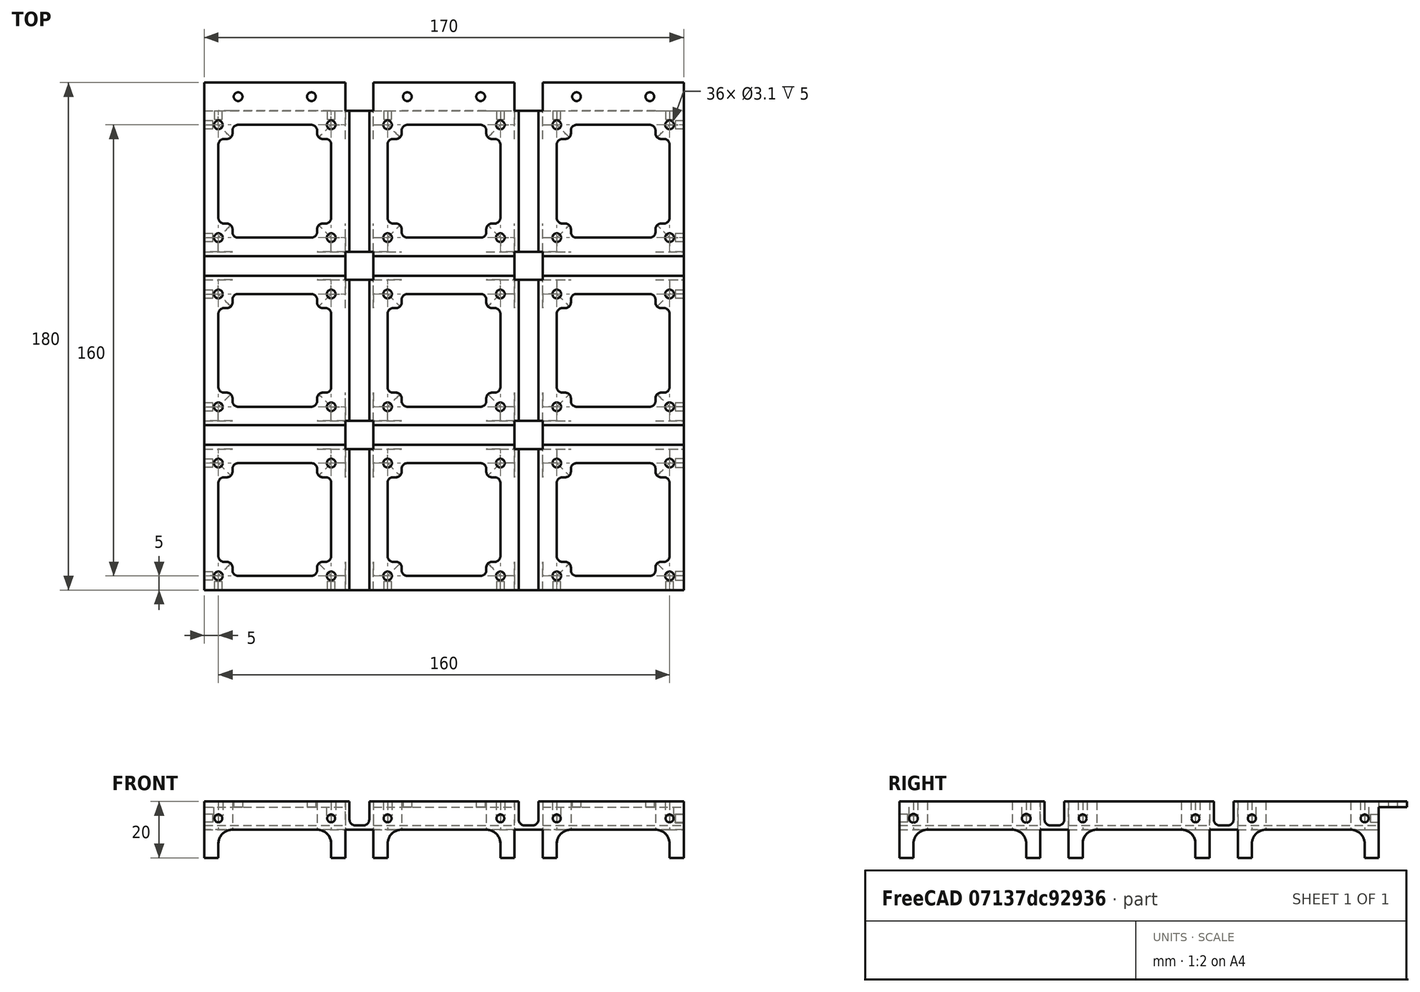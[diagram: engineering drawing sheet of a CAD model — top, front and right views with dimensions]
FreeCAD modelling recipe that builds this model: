
FCSTD DOCUMENT  (FreeCAD 0.20R29603 (Git))
Label: BackplaneLeft
License: All rights reserved
LicenseURL: http://en.wikipedia.org/wiki/All_rights_reserved
objects: Sketcher::SketchObject×59, PartDesign::Pocket×49, App::Link×13, PartDesign::Pad×10, PartDesign::Body×10, Part::Cylinder×2, Part::Cut×2, Part::Box×1, App::Part×1, Part::MultiFuse×1, Mesh::Feature×1
note: 193 computed .brp shape members not serialized (recipe doc carries the construction recipe); baked Part::Feature solids carry a one-line shape summary decoded from their .brp

FEATURE [Sketcher::SketchObject] Sketch
  FullyConstrained = true
  MapMode = 5
  Placement = pos=(0,0,0) rot=(0.57735,0.57735,0.57735;2.0944rad)
  Support = -> [YZ_Plane001]
  sketch-geometry (4):
    g0: LineSegment StartX=0 StartY=0 StartZ=0 EndX=10 EndY=0 EndZ=0
    g1: LineSegment StartX=10 StartY=0 StartZ=0 EndX=10 EndY=10 EndZ=0
    g2: LineSegment StartX=10 StartY=10 StartZ=0 EndX=0 EndY=10 EndZ=0
    g3: LineSegment StartX=0 StartY=10 StartZ=0 EndX=0 EndY=0 EndZ=0
  constraints (11):
    c: Coincident(g0,g1)
    c: Coincident(g1,g2)
    c: Coincident(g2,g3)
    c: Coincident(g3,g0)
    c: Horizontal(g0)
    c: Horizontal(g2)
    c: Vertical(g1)
    c: Vertical(g3)
    c: Coincident(g0,g-1)
    c: DistanceY(g3,g3) = 10
    c: DistanceX(g2,g2) = 10
FEATURE [PartDesign::Pad] Pad
  Direction = (1,-2e-16,3e-16)
  Length = 50
  Length2 = 10
  Placement = pos=(0,0,0) rot=(0.57735,0.57735,0.57735;2.0944rad)
  Profile = -> Sketch
  ReferenceAxis = -> Sketch [N_Axis]
  Type = 0
FEATURE [Sketcher::SketchObject] Sketch001
  ExternalGeometry = -> [Pad]
  FullyConstrained = true
  MapMode = 5
  Placement = pos=(0,0,0) rot=(0.57735,0.57735,-0.57735;4.18879rad)
  Support = -> [Pad]
  sketch-geometry (6):
    g0: LineSegment StartX=8.5 StartY=-10 StartZ=0 EndX=8.5 EndY=-3.5 EndZ=0
    g1: LineSegment StartX=6.5 StartY=-1.5 StartZ=0 EndX=3.5 EndY=-1.5 EndZ=0
    g2: LineSegment StartX=1.5 StartY=-3.5 StartZ=0 EndX=1.5 EndY=-10 EndZ=0
    g3: ArcOfCircle CenterX=6.5 CenterY=-3.5 CenterZ=0 NormalX=0 NormalY=0 NormalZ=1 AngleXU=0 Radius=2 StartAngle=1e-16 EndAngle=1.5708
    g4: ArcOfCircle CenterX=3.5 CenterY=-3.5 CenterZ=0 NormalX=0 NormalY=0 NormalZ=1 AngleXU=0 Radius=2 StartAngle=1.5708 EndAngle=3.14159
    g5: LineSegment StartX=1.5 StartY=-10 StartZ=0 EndX=8.5 EndY=-10 EndZ=0
  constraints (16):
    c: PointOnObject(g0,g-3)
    c: Vertical(g0)
    c: Horizontal(g1)
    c: PointOnObject(g2,g-3)
    c: Vertical(g2)
    c: Tangent(g0,g3) = -1.5708
    c: Tangent(g1,g3) = -1.5708
    c: Tangent(g1,g4) = -1.5708
    c: Tangent(g2,g4) = -1.5708
    c: Radius(g4) = 2
    c: Radius(g3) = 2
    c: Distance(g2,g-5) = 1.5
    c: Distance(g0,g-4) = 1.5
    c: Distance(g1,g-6) = 1.5
    c: Coincident(g5,g2)
    c: Coincident(g5,g0)
FEATURE [PartDesign::Pocket] Pocket
  BaseFeature = -> Pad
  Direction = (1,-4e-16,4e-16)
  Length = 5
  Length2 = 5
  Placement = pos=(0,0,0) rot=(0.57735,0.57735,0.57735;2.0944rad)
  Profile = -> Sketch001
  ReferenceAxis = -> Sketch001 [N_Axis]
  Type = 1
FEATURE [PartDesign::Body] Body  label="BackplaneChannel"
  Group = -> [Sketch,Pad,Sketch001,Pocket]
  Origin = -> Origin001
  Placement = pos=(0,50,10) rot=(0,0,1;0rad)
  Tip = -> Pocket
FEATURE [App::Link] Link008  label="BackplaneChannel001"
  LinkPlacement = pos=(60,50,10) rot=(0,0,1;0rad)
  LinkedObject = -> Body
  Placement = pos=(60,50,10) rot=(0,0,1;0rad)
FEATURE [App::Link] Link009  label="BackplaneChannel002"
  LinkPlacement = pos=(120,50,10) rot=(0,0,1;0rad)
  LinkedObject = -> Body
  Placement = pos=(120,50,10) rot=(0,0,1;0rad)
FEATURE [App::Link] Link010  label="BackplaneChannel003"
  LinkPlacement = pos=(0,110,10) rot=(0,0,1;0rad)
  LinkedObject = -> Body
  Placement = pos=(0,110,10) rot=(0,0,1;0rad)
FEATURE [App::Link] Link011  label="BackplaneChannel004"
  LinkPlacement = pos=(60,110,10) rot=(0,0,1;0rad)
  LinkedObject = -> Body
  Placement = pos=(60,110,10) rot=(0,0,1;0rad)
FEATURE [App::Link] Link012  label="BackplaneChannel005"
  LinkPlacement = pos=(120,110,10) rot=(0,0,1;0rad)
  LinkedObject = -> Body
  Placement = pos=(120,110,10) rot=(0,0,1;0rad)
FEATURE [App::Link] Link013  label="BackplaneChannel006"
  LinkPlacement = pos=(60,0,10) rot=(0,0,1;1.5708rad)
  LinkedObject = -> Body
  Placement = pos=(60,0,10) rot=(0,0,1;1.5708rad)
FEATURE [App::Link] Link014  label="BackplaneChannel007"
  LinkPlacement = pos=(120,0,10) rot=(0,0,1;1.5708rad)
  LinkedObject = -> Body
  Placement = pos=(120,0,10) rot=(0,0,1;1.5708rad)
FEATURE [App::Link] Link015  label="BackplaneChannel008"
  LinkPlacement = pos=(60,60,10) rot=(0,0,1;1.5708rad)
  LinkedObject = -> Body
  Placement = pos=(60,60,10) rot=(0,0,1;1.5708rad)
FEATURE [App::Link] Link016  label="BackplaneChannel009"
  LinkPlacement = pos=(60,120,10) rot=(0,0,1;1.5708rad)
  LinkedObject = -> Body
  Placement = pos=(60,120,10) rot=(0,0,1;1.5708rad)
FEATURE [App::Link] Link017  label="BackplaneChannel010"
  LinkPlacement = pos=(120,60,10) rot=(0,0,1;1.5708rad)
  LinkedObject = -> Body
  Placement = pos=(120,60,10) rot=(0,0,1;1.5708rad)
FEATURE [App::Link] Link018  label="BackplaneChannel011"
  LinkPlacement = pos=(120,120,10) rot=(0,0,1;1.5708rad)
  LinkedObject = -> Body
  Placement = pos=(120,120,10) rot=(0,0,1;1.5708rad)
FEATURE [Sketcher::SketchObject] Sketch002
  FullyConstrained = true
  MapMode = 5
  Support = -> [XY_Plane002]
  sketch-geometry (4):
    g0: LineSegment StartX=-25 StartY=25 StartZ=0 EndX=25 EndY=25 EndZ=0
    g1: LineSegment StartX=25 StartY=25 StartZ=0 EndX=25 EndY=-25 EndZ=0
    g2: LineSegment StartX=25 StartY=-25 StartZ=0 EndX=-25 EndY=-25 EndZ=0
    g3: LineSegment StartX=-25 StartY=-25 StartZ=0 EndX=-25 EndY=25 EndZ=0
  constraints (10):
    c: Coincident(g0,g1)
    c: Coincident(g1,g2)
    c: Coincident(g2,g3)
    c: Coincident(g3,g0)
    c: Horizontal(g0)
    c: Vertical(g3)
    c: Symmetric(g2,g1,g-2)
    c: Symmetric(g1,g0,g-1)
    c: DistanceY(g1,g1) = 50
    c: DistanceX(g2,g2) = 50
FEATURE [PartDesign::Pad] Pad001
  Direction = (0,0,1)
  Length = 20
  Length2 = 10
  Profile = -> Sketch002
  ReferenceAxis = -> Sketch002 [N_Axis]
  Type = 0
FEATURE [Sketcher::SketchObject] Sketch003
  ExternalGeometry = -> [Pad001]
  FullyConstrained = true
  MapMode = 5
  Placement = pos=(0,0,20) rot=(0,0,1;0rad)
  Support = -> [Pad001]
  sketch-geometry (36):
    g0: LineSegment StartX=-18 StartY=15 StartZ=0 EndX=-17 EndY=15 EndZ=0
    g1: LineSegment StartX=20 StartY=13 StartZ=0 EndX=20 EndY=-13 EndZ=0
    g2: LineSegment StartX=18 StartY=-15 StartZ=0 EndX=17 EndY=-15 EndZ=0
    g3: LineSegment StartX=-20 StartY=-13 StartZ=0 EndX=-20 EndY=13 EndZ=0
    g4: LineSegment StartX=-13 StartY=20 StartZ=0 EndX=13 EndY=20 EndZ=0
    g5: LineSegment StartX=15 StartY=18 StartZ=0 EndX=15 EndY=17 EndZ=0
    g6: LineSegment StartX=13 StartY=-20 StartZ=0 EndX=-13 EndY=-20 EndZ=0
    g7: LineSegment StartX=-15 StartY=-18 StartZ=0 EndX=-15 EndY=-17 EndZ=0
    g8: LineSegment StartX=17 StartY=15 StartZ=0 EndX=18 EndY=15 EndZ=0
    g9: LineSegment StartX=-15 StartY=17 StartZ=0 EndX=-15 EndY=18 EndZ=0
    g10: LineSegment StartX=-17 StartY=-15 StartZ=0 EndX=-18 EndY=-15 EndZ=0
    g11: LineSegment StartX=15 StartY=-17 StartZ=0 EndX=15 EndY=-18 EndZ=0
    g12: ArcOfCircle CenterX=-13 CenterY=-18 CenterZ=0 NormalX=0 NormalY=0 NormalZ=1 AngleXU=0 Radius=2 StartAngle=3.14159 EndAngle=4.71239
    g13: GeomPoint X=-15 Y=-20 Z=0
    g14: ArcOfCircle CenterX=13 CenterY=-18 CenterZ=0 NormalX=0 NormalY=0 NormalZ=1 AngleXU=0 Radius=2 StartAngle=4.71239 EndAngle=6.28319
    g15: GeomPoint X=15 Y=-20 Z=0
    g16: ArcOfCircle CenterX=17 CenterY=-17 CenterZ=0 NormalX=0 NormalY=0 NormalZ=1 AngleXU=0 Radius=2 StartAngle=1.5708 EndAngle=3.14159
    g17: GeomPoint X=15 Y=-15 Z=0
    g18: ArcOfCircle CenterX=18 CenterY=-13 CenterZ=0 NormalX=0 NormalY=0 NormalZ=1 AngleXU=0 Radius=2 StartAngle=4.71239 EndAngle=6.28319
    g19: GeomPoint X=20 Y=-15 Z=0
    g20: ArcOfCircle CenterX=18 CenterY=13 CenterZ=0 NormalX=0 NormalY=0 NormalZ=1 AngleXU=0 Radius=2 StartAngle=0 EndAngle=1.5708
    g21: GeomPoint X=20 Y=15 Z=0
    g22: ArcOfCircle CenterX=17 CenterY=17 CenterZ=0 NormalX=0 NormalY=0 NormalZ=1 AngleXU=0 Radius=2 StartAngle=3.14159 EndAngle=4.71239
    g23: GeomPoint X=15 Y=15 Z=0
    g24: ArcOfCircle CenterX=13 CenterY=18 CenterZ=0 NormalX=0 NormalY=0 NormalZ=1 AngleXU=0 Radius=2 StartAngle=4e-16 EndAngle=1.5708
    g25: GeomPoint X=15 Y=20 Z=0
    g26: ArcOfCircle CenterX=-13 CenterY=18 CenterZ=0 NormalX=0 NormalY=0 NormalZ=1 AngleXU=0 Radius=2 StartAngle=1.5708 EndAngle=3.14159
    g27: GeomPoint X=-15 Y=20 Z=0
    g28: ArcOfCircle CenterX=-17 CenterY=17 CenterZ=0 NormalX=0 NormalY=0 NormalZ=1 AngleXU=0 Radius=2 StartAngle=4.71239 EndAngle=6.28319
    g29: GeomPoint X=-15 Y=15 Z=0
    g30: ArcOfCircle CenterX=-18 CenterY=13 CenterZ=0 NormalX=0 NormalY=0 NormalZ=1 AngleXU=0 Radius=2 StartAngle=1.5708 EndAngle=3.14159
    g31: GeomPoint X=-20 Y=15 Z=0
    g32: ArcOfCircle CenterX=-18 CenterY=-13 CenterZ=0 NormalX=0 NormalY=0 NormalZ=1 AngleXU=0 Radius=2 StartAngle=3.14159 EndAngle=4.71239
    g33: GeomPoint X=-20 Y=-15 Z=0
    g34: ArcOfCircle CenterX=-17 CenterY=-17 CenterZ=0 NormalX=0 NormalY=0 NormalZ=1 AngleXU=0 Radius=2 StartAngle=0 EndAngle=1.5708
    g35: GeomPoint X=-15 Y=-15 Z=0
  constraints (80):
    c: Horizontal(g2)
    c: Vertical(g3)
    c: Symmetric(g21,g31,g-2)
    c: Symmetric(g21,g19,g-1)
    c: DistanceX(g31,g21) = 40
    c: DistanceY(g19,g21) = 30
    c: Horizontal(g4)
    c: Vertical(g7)
    c: Symmetric(g13,g15,g-2)
    c: Symmetric(g15,g25,g-1)
    c: DistanceY(g15,g25) = 40
    c: Vertical(g9)
    c: Vertical(g5)
    c: Vertical(g11)
    c: Horizontal(g10)
    c: Horizontal(g8)
    c: Horizontal(g0)
    c: DistanceX(g13,g15) = 30
    c: DistanceY(g33,g31) = 30
    c: DistanceX(g27,g25) = 30
    c: PointOnObject(g13,g7)
    c: PointOnObject(g13,g6)
    c: Tangent(g7,g12) = 1.5708
    c: Tangent(g6,g12) = 1.5708
    c: Radius(g12) = 2
    c: PointOnObject(g15,g11)
    c: PointOnObject(g15,g6)
    c: Tangent(g11,g14) = 1.5708
    c: Tangent(g6,g14) = 1.5708
    c: PointOnObject(g17,g11)
    c: PointOnObject(g17,g2)
    c: Tangent(g11,g16) = -1.5708
    c: Tangent(g2,g16) = -1.5708
    c: PointOnObject(g19,g2)
    c: PointOnObject(g19,g1)
    c: Tangent(g2,g18) = 1.5708
    c: Tangent(g1,g18) = 1.5708
    c: PointOnObject(g21,g1)
    c: PointOnObject(g21,g8)
    c: Tangent(g1,g20) = 1.5708
    c: Tangent(g8,g20) = 1.5708
    c: PointOnObject(g23,g8)
    c: PointOnObject(g23,g5)
    c: Tangent(g8,g22) = -1.5708
    c: Tangent(g5,g22) = -1.5708
    c: PointOnObject(g25,g5)
    c: PointOnObject(g25,g4)
    c: Tangent(g5,g24) = 1.5708
    c: Tangent(g4,g24) = 1.5708
    c: PointOnObject(g27,g9)
    c: PointOnObject(g27,g4)
    c: Tangent(g9,g26) = 1.5708
    c: Tangent(g4,g26) = 1.5708
    c: PointOnObject(g29,g9)
    c: PointOnObject(g29,g0)
    c: Tangent(g9,g28) = -1.5708
    c: Tangent(g0,g28) = -1.5708
    c: PointOnObject(g31,g0)
    c: PointOnObject(g31,g3)
    c: Tangent(g0,g30) = 1.5708
    c: Tangent(g3,g30) = 1.5708
    c: PointOnObject(g33,g3)
    c: PointOnObject(g33,g10)
    c: Tangent(g3,g32) = 1.5708
    c: Tangent(g10,g32) = 1.5708
    c: PointOnObject(g35,g10)
    c: PointOnObject(g35,g7)
    c: Tangent(g10,g34) = -1.5708
    c: Tangent(g7,g34) = -1.5708
    c: Radius(g34) = 2
    c: Radius(g32) = 2
    c: Radius(g30) = 2
    c: Radius(g28) = 2
    c: Radius(g26) = 2
    c: Radius(g24) = 2
    c: Radius(g22) = 2
    c: Radius(g20) = 2
    c: Radius(g18) = 2
    c: Radius(g16) = 2
    c: Radius(g14) = 2
FEATURE [PartDesign::Pocket] Pocket001
  BaseFeature = -> Pad001
  Direction = (0,0,-1)
  Length = 5
  Length2 = 5
  Profile = -> Sketch003
  ReferenceAxis = -> Sketch003 [N_Axis]
  Type = 1
FEATURE [Sketcher::SketchObject] Sketch004
  ExternalGeometry = -> [Pocket001]
  FullyConstrained = true
  MapMode = 5
  Placement = pos=(25,0,0) rot=(0.57735,0.57735,0.57735;2.0944rad)
  Support = -> [Pocket001]
  sketch-geometry (6):
    g0: LineSegment StartX=-15 StartY=10 StartZ=0 EndX=15 EndY=10 EndZ=0
    g1: LineSegment StartX=20 StartY=5 StartZ=0 EndX=20 EndY=0 EndZ=0
    g2: LineSegment StartX=20 StartY=0 StartZ=0 EndX=-20 EndY=0 EndZ=0
    g3: LineSegment StartX=-20 StartY=0 StartZ=0 EndX=-20 EndY=5 EndZ=0
    g4: ArcOfCircle CenterX=15 CenterY=5 CenterZ=0 NormalX=0 NormalY=0 NormalZ=1 AngleXU=0 Radius=5 StartAngle=1.11001e-11 EndAngle=1.5708
    g5: ArcOfCircle CenterX=-15 CenterY=5 CenterZ=0 NormalX=0 NormalY=0 NormalZ=1 AngleXU=0 Radius=5 StartAngle=1.5708 EndAngle=3.14159
  constraints (15):
    c: Coincident(g1,g2)
    c: Coincident(g2,g3)
    c: Vertical(g1)
    c: Vertical(g3)
    c: PointOnObject(g1,g-1)
    c: Tangent(g1,g4) = 1.5708
    c: Tangent(g0,g4) = 1.5708
    c: Tangent(g0,g5) = 1.5708
    c: Tangent(g3,g5) = 1.5708
    c: Horizontal(g0)
    c: DistanceX(g2,g2) = 40
    c: Symmetric(g2,g1,g-2)
    c: Distance(g-1,g0) = 10
    c: Radius(g5) = 5
    c: Radius(g4) = 5
FEATURE [PartDesign::Pocket] Pocket002
  BaseFeature = -> Pocket001
  Direction = (-1,0,0)
  Length = 5
  Length2 = 5
  Profile = -> Sketch004
  ReferenceAxis = -> Sketch004 [N_Axis]
  Type = 1
FEATURE [Sketcher::SketchObject] Sketch005
  FullyConstrained = true
  MapMode = 5
  Placement = pos=(0,-25,0) rot=(1,0,0;1.5708rad)
  Support = -> [Pocket001]
  sketch-geometry (6):
    g0: LineSegment StartX=-15 StartY=10 StartZ=0 EndX=15 EndY=10 EndZ=0
    g1: LineSegment StartX=20 StartY=5 StartZ=0 EndX=20 EndY=0 EndZ=0
    g2: LineSegment StartX=20 StartY=0 StartZ=0 EndX=-20 EndY=0 EndZ=0
    g3: LineSegment StartX=-20 StartY=0 StartZ=0 EndX=-20 EndY=5 EndZ=0
    g4: ArcOfCircle CenterX=15 CenterY=5 CenterZ=0 NormalX=0 NormalY=0 NormalZ=1 AngleXU=0 Radius=5 StartAngle=1.11e-11 EndAngle=1.5708
    g5: ArcOfCircle CenterX=-15 CenterY=5 CenterZ=0 NormalX=0 NormalY=0 NormalZ=1 AngleXU=0 Radius=5 StartAngle=1.5708 EndAngle=3.14159
  constraints (15):
    c: Coincident(g1,g2)
    c: Coincident(g2,g3)
    c: Horizontal(g0)
    c: Vertical(g1)
    c: Vertical(g3)
    c: Symmetric(g2,g1,g-2)
    c: PointOnObject(g1,g-1)
    c: Tangent(g0,g4) = 1.5708
    c: Tangent(g1,g4) = 1.5708
    c: Tangent(g0,g5) = 1.5708
    c: Tangent(g3,g5) = 1.5708
    c: DistanceX(g2,g2) = 40
    c: Distance(g-1,g0) = 10
    c: Radius(g5) = 5
    c: Radius(g4) = 5
FEATURE [PartDesign::Pocket] Pocket003
  BaseFeature = -> Pocket002
  Direction = (0,1,-2e-16)
  Length = 5
  Length2 = 5
  Profile = -> Sketch005
  ReferenceAxis = -> Sketch005 [N_Axis]
  Type = 1
FEATURE [Sketcher::SketchObject] Sketch009
  FullyConstrained = false
  MapMode = 5
  Placement = pos=(0,0,20) rot=(0,0,1;0rad)
  sketch-geometry (4):
    g0: Circle CenterX=-20 CenterY=20 CenterZ=0 NormalX=0 NormalY=0 NormalZ=1 AngleXU=0 Radius=1.55
    g1: Circle CenterX=20 CenterY=20 CenterZ=0 NormalX=0 NormalY=0 NormalZ=1 AngleXU=0 Radius=1.55
    g2: Circle CenterX=20 CenterY=-20 CenterZ=0 NormalX=0 NormalY=0 NormalZ=1 AngleXU=0 Radius=1.55
    g3: Circle CenterX=-20 CenterY=-20 CenterZ=0 NormalX=0 NormalY=0 NormalZ=1 AngleXU=0 Radius=1.55
  constraints (4):
    c: Diameter(g0) = 3.1
    c: Diameter(g1) = 3.1
    c: Diameter(g2) = 3.1
    c: Diameter(g3) = 3.1
FEATURE [PartDesign::Pocket] Pocket008
  BaseFeature = -> Pocket003
  Direction = (0,0,-1)
  Length = 5
  Length2 = 5
  Profile = -> Sketch009
  ReferenceAxis = -> Sketch009 [N_Axis]
  Type = 0
FEATURE [Sketcher::SketchObject] Sketch010
  FullyConstrained = true
  MapMode = 5
  Support = -> [XY_Plane003]
  sketch-geometry (4):
    g0: LineSegment StartX=-25 StartY=25 StartZ=0 EndX=25 EndY=25 EndZ=0
    g1: LineSegment StartX=25 StartY=25 StartZ=0 EndX=25 EndY=-25 EndZ=0
    g2: LineSegment StartX=25 StartY=-25 StartZ=0 EndX=-25 EndY=-25 EndZ=0
    g3: LineSegment StartX=-25 StartY=-25 StartZ=0 EndX=-25 EndY=25 EndZ=0
  constraints (10):
    c: Coincident(g0,g1)
    c: Coincident(g1,g2)
    c: Coincident(g2,g3)
    c: Coincident(g3,g0)
    c: Horizontal(g0)
    c: Vertical(g3)
    c: Symmetric(g2,g1,g-2)
    c: Symmetric(g1,g0,g-1)
    c: DistanceY(g1,g1) = 50
    c: DistanceX(g2,g2) = 50
FEATURE [PartDesign::Pad] Pad002
  Direction = (0,0,1)
  Length = 20
  Length2 = 10
  Profile = -> Sketch010
  ReferenceAxis = -> Sketch010 [N_Axis]
  Type = 0
FEATURE [Sketcher::SketchObject] Sketch011
  ExternalGeometry = -> [Pad002]
  FullyConstrained = true
  MapMode = 5
  Placement = pos=(0,0,20) rot=(0,0,1;0rad)
  Support = -> [Pad002]
  sketch-geometry (36):
    g0: LineSegment StartX=-18 StartY=15 StartZ=0 EndX=-17 EndY=15 EndZ=0
    g1: LineSegment StartX=20 StartY=13 StartZ=0 EndX=20 EndY=-13 EndZ=0
    g2: LineSegment StartX=18 StartY=-15 StartZ=0 EndX=17 EndY=-15 EndZ=0
    g3: LineSegment StartX=-20 StartY=-13 StartZ=0 EndX=-20 EndY=13 EndZ=0
    g4: LineSegment StartX=-13 StartY=20 StartZ=0 EndX=13 EndY=20 EndZ=0
    g5: LineSegment StartX=15 StartY=18 StartZ=0 EndX=15 EndY=17 EndZ=0
    g6: LineSegment StartX=13 StartY=-20 StartZ=0 EndX=-13 EndY=-20 EndZ=0
    g7: LineSegment StartX=-15 StartY=-18 StartZ=0 EndX=-15 EndY=-17 EndZ=0
    g8: LineSegment StartX=17 StartY=15 StartZ=0 EndX=18 EndY=15 EndZ=0
    g9: LineSegment StartX=-15 StartY=17 StartZ=0 EndX=-15 EndY=18 EndZ=0
    g10: LineSegment StartX=-17 StartY=-15 StartZ=0 EndX=-18 EndY=-15 EndZ=0
    g11: LineSegment StartX=15 StartY=-17 StartZ=0 EndX=15 EndY=-18 EndZ=0
    g12: ArcOfCircle CenterX=-13 CenterY=-18 CenterZ=0 NormalX=0 NormalY=0 NormalZ=1 AngleXU=0 Radius=2 StartAngle=3.14159 EndAngle=4.71239
    g13: GeomPoint X=-15 Y=-20 Z=0
    g14: ArcOfCircle CenterX=13 CenterY=-18 CenterZ=0 NormalX=0 NormalY=0 NormalZ=1 AngleXU=0 Radius=2 StartAngle=4.71239 EndAngle=6.28319
    g15: GeomPoint X=15 Y=-20 Z=0
    g16: ArcOfCircle CenterX=17 CenterY=-17 CenterZ=0 NormalX=0 NormalY=0 NormalZ=1 AngleXU=0 Radius=2 StartAngle=1.5708 EndAngle=3.14159
    g17: GeomPoint X=15 Y=-15 Z=0
    g18: ArcOfCircle CenterX=18 CenterY=-13 CenterZ=0 NormalX=0 NormalY=0 NormalZ=1 AngleXU=0 Radius=2 StartAngle=4.71239 EndAngle=6.28319
    g19: GeomPoint X=20 Y=-15 Z=0
    g20: ArcOfCircle CenterX=18 CenterY=13 CenterZ=0 NormalX=0 NormalY=0 NormalZ=1 AngleXU=0 Radius=2 StartAngle=0 EndAngle=1.5708
    g21: GeomPoint X=20 Y=15 Z=0
    g22: ArcOfCircle CenterX=17 CenterY=17 CenterZ=0 NormalX=0 NormalY=0 NormalZ=1 AngleXU=0 Radius=2 StartAngle=3.14159 EndAngle=4.71239
    g23: GeomPoint X=15 Y=15 Z=0
    g24: ArcOfCircle CenterX=13 CenterY=18 CenterZ=0 NormalX=0 NormalY=0 NormalZ=1 AngleXU=0 Radius=2 StartAngle=4e-16 EndAngle=1.5708
    g25: GeomPoint X=15 Y=20 Z=0
    g26: ArcOfCircle CenterX=-13 CenterY=18 CenterZ=0 NormalX=0 NormalY=0 NormalZ=1 AngleXU=0 Radius=2 StartAngle=1.5708 EndAngle=3.14159
    g27: GeomPoint X=-15 Y=20 Z=0
    g28: ArcOfCircle CenterX=-17 CenterY=17 CenterZ=0 NormalX=0 NormalY=0 NormalZ=1 AngleXU=0 Radius=2 StartAngle=4.71239 EndAngle=6.28319
    g29: GeomPoint X=-15 Y=15 Z=0
    g30: ArcOfCircle CenterX=-18 CenterY=13 CenterZ=0 NormalX=0 NormalY=0 NormalZ=1 AngleXU=0 Radius=2 StartAngle=1.5708 EndAngle=3.14159
    g31: GeomPoint X=-20 Y=15 Z=0
    g32: ArcOfCircle CenterX=-18 CenterY=-13 CenterZ=0 NormalX=0 NormalY=0 NormalZ=1 AngleXU=0 Radius=2 StartAngle=3.14159 EndAngle=4.71239
    g33: GeomPoint X=-20 Y=-15 Z=0
    g34: ArcOfCircle CenterX=-17 CenterY=-17 CenterZ=0 NormalX=0 NormalY=0 NormalZ=1 AngleXU=0 Radius=2 StartAngle=0 EndAngle=1.5708
    g35: GeomPoint X=-15 Y=-15 Z=0
  constraints (80):
    c: Horizontal(g2)
    c: Vertical(g3)
    c: Symmetric(g21,g31,g-2)
    c: Symmetric(g21,g19,g-1)
    c: DistanceX(g31,g21) = 40
    c: DistanceY(g19,g21) = 30
    c: Horizontal(g4)
    c: Vertical(g7)
    c: Symmetric(g13,g15,g-2)
    c: Symmetric(g15,g25,g-1)
    c: DistanceY(g15,g25) = 40
    c: Vertical(g9)
    c: Vertical(g5)
    c: Vertical(g11)
    c: Horizontal(g10)
    c: Horizontal(g8)
    c: Horizontal(g0)
    c: DistanceX(g13,g15) = 30
    c: DistanceY(g33,g31) = 30
    c: DistanceX(g27,g25) = 30
    c: PointOnObject(g13,g7)
    c: PointOnObject(g13,g6)
    c: Tangent(g7,g12) = 1.5708
    c: Tangent(g6,g12) = 1.5708
    c: Radius(g12) = 2
    c: PointOnObject(g15,g11)
    c: PointOnObject(g15,g6)
    c: Tangent(g11,g14) = 1.5708
    c: Tangent(g6,g14) = 1.5708
    c: PointOnObject(g17,g11)
    c: PointOnObject(g17,g2)
    c: Tangent(g11,g16) = -1.5708
    c: Tangent(g2,g16) = -1.5708
    c: PointOnObject(g19,g2)
    c: PointOnObject(g19,g1)
    c: Tangent(g2,g18) = 1.5708
    c: Tangent(g1,g18) = 1.5708
    c: PointOnObject(g21,g1)
    c: PointOnObject(g21,g8)
    c: Tangent(g1,g20) = 1.5708
    c: Tangent(g8,g20) = 1.5708
    c: PointOnObject(g23,g8)
    c: PointOnObject(g23,g5)
    c: Tangent(g8,g22) = -1.5708
    c: Tangent(g5,g22) = -1.5708
    c: PointOnObject(g25,g5)
    c: PointOnObject(g25,g4)
    c: Tangent(g5,g24) = 1.5708
    c: Tangent(g4,g24) = 1.5708
    c: PointOnObject(g27,g9)
    c: PointOnObject(g27,g4)
    c: Tangent(g9,g26) = 1.5708
    c: Tangent(g4,g26) = 1.5708
    c: PointOnObject(g29,g9)
    c: PointOnObject(g29,g0)
    c: Tangent(g9,g28) = -1.5708
    c: Tangent(g0,g28) = -1.5708
    c: PointOnObject(g31,g0)
    c: PointOnObject(g31,g3)
    c: Tangent(g0,g30) = 1.5708
    c: Tangent(g3,g30) = 1.5708
    c: PointOnObject(g33,g3)
    c: PointOnObject(g33,g10)
    c: Tangent(g3,g32) = 1.5708
    c: Tangent(g10,g32) = 1.5708
    c: PointOnObject(g35,g10)
    c: PointOnObject(g35,g7)
    c: Tangent(g10,g34) = -1.5708
    c: Tangent(g7,g34) = -1.5708
    c: Radius(g34) = 2
    c: Radius(g32) = 2
    c: Radius(g30) = 2
    c: Radius(g28) = 2
    c: Radius(g26) = 2
    c: Radius(g24) = 2
    c: Radius(g22) = 2
    c: Radius(g20) = 2
    c: Radius(g18) = 2
    c: Radius(g16) = 2
    c: Radius(g14) = 2
FEATURE [PartDesign::Pocket] Pocket009
  BaseFeature = -> Pad002
  Direction = (0,0,-1)
  Length = 5
  Length2 = 5
  Profile = -> Sketch011
  ReferenceAxis = -> Sketch011 [N_Axis]
  Type = 1
FEATURE [Sketcher::SketchObject] Sketch012
  ExternalGeometry = -> [Pocket009]
  FullyConstrained = true
  MapMode = 5
  Placement = pos=(25,0,0) rot=(0.57735,0.57735,0.57735;2.0944rad)
  Support = -> [Pocket009]
  sketch-geometry (6):
    g0: LineSegment StartX=-15 StartY=10 StartZ=0 EndX=15 EndY=10 EndZ=0
    g1: LineSegment StartX=20 StartY=5 StartZ=0 EndX=20 EndY=0 EndZ=0
    g2: LineSegment StartX=20 StartY=0 StartZ=0 EndX=-20 EndY=0 EndZ=0
    g3: LineSegment StartX=-20 StartY=0 StartZ=0 EndX=-20 EndY=5 EndZ=0
    g4: ArcOfCircle CenterX=15 CenterY=5 CenterZ=0 NormalX=0 NormalY=0 NormalZ=1 AngleXU=0 Radius=5 StartAngle=1.11001e-11 EndAngle=1.5708
    g5: ArcOfCircle CenterX=-15 CenterY=5 CenterZ=0 NormalX=0 NormalY=0 NormalZ=1 AngleXU=0 Radius=5 StartAngle=1.5708 EndAngle=3.14159
  constraints (15):
    c: Coincident(g1,g2)
    c: Coincident(g2,g3)
    c: Vertical(g1)
    c: Vertical(g3)
    c: PointOnObject(g1,g-1)
    c: Tangent(g1,g4) = 1.5708
    c: Tangent(g0,g4) = 1.5708
    c: Tangent(g0,g5) = 1.5708
    c: Tangent(g3,g5) = 1.5708
    c: Horizontal(g0)
    c: DistanceX(g2,g2) = 40
    c: Symmetric(g2,g1,g-2)
    c: Distance(g-1,g0) = 10
    c: Radius(g5) = 5
    c: Radius(g4) = 5
FEATURE [PartDesign::Pocket] Pocket010
  BaseFeature = -> Pocket009
  Direction = (-1,0,0)
  Length = 5
  Length2 = 5
  Profile = -> Sketch012
  ReferenceAxis = -> Sketch012 [N_Axis]
  Type = 1
FEATURE [Sketcher::SketchObject] Sketch013
  FullyConstrained = true
  MapMode = 5
  Placement = pos=(0,-25,0) rot=(1,0,0;1.5708rad)
  Support = -> [Pocket009]
  sketch-geometry (6):
    g0: LineSegment StartX=-15 StartY=10 StartZ=0 EndX=15 EndY=10 EndZ=0
    g1: LineSegment StartX=20 StartY=5 StartZ=0 EndX=20 EndY=0 EndZ=0
    g2: LineSegment StartX=20 StartY=0 StartZ=0 EndX=-20 EndY=0 EndZ=0
    g3: LineSegment StartX=-20 StartY=0 StartZ=0 EndX=-20 EndY=5 EndZ=0
    g4: ArcOfCircle CenterX=15 CenterY=5 CenterZ=0 NormalX=0 NormalY=0 NormalZ=1 AngleXU=0 Radius=5 StartAngle=1.11e-11 EndAngle=1.5708
    g5: ArcOfCircle CenterX=-15 CenterY=5 CenterZ=0 NormalX=0 NormalY=0 NormalZ=1 AngleXU=0 Radius=5 StartAngle=1.5708 EndAngle=3.14159
  constraints (15):
    c: Coincident(g1,g2)
    c: Coincident(g2,g3)
    c: Horizontal(g0)
    c: Vertical(g1)
    c: Vertical(g3)
    c: Symmetric(g2,g1,g-2)
    c: PointOnObject(g1,g-1)
    c: Tangent(g0,g4) = 1.5708
    c: Tangent(g1,g4) = 1.5708
    c: Tangent(g0,g5) = 1.5708
    c: Tangent(g3,g5) = 1.5708
    c: DistanceX(g2,g2) = 40
    c: Distance(g-1,g0) = 10
    c: Radius(g5) = 5
    c: Radius(g4) = 5
FEATURE [PartDesign::Pocket] Pocket011
  BaseFeature = -> Pocket010
  Direction = (0,1,-2e-16)
  Length = 5
  Length2 = 5
  Profile = -> Sketch013
  ReferenceAxis = -> Sketch013 [N_Axis]
  Type = 1
FEATURE [Sketcher::SketchObject] Sketch014
  FullyConstrained = false
  MapMode = 5
  Placement = pos=(0,0,20) rot=(0,0,1;0rad)
  sketch-geometry (4):
    g0: Circle CenterX=-20 CenterY=20 CenterZ=0 NormalX=0 NormalY=0 NormalZ=1 AngleXU=0 Radius=1.55
    g1: Circle CenterX=20 CenterY=20 CenterZ=0 NormalX=0 NormalY=0 NormalZ=1 AngleXU=0 Radius=1.55
    g2: Circle CenterX=20 CenterY=-20 CenterZ=0 NormalX=0 NormalY=0 NormalZ=1 AngleXU=0 Radius=1.55
    g3: Circle CenterX=-20 CenterY=-20 CenterZ=0 NormalX=0 NormalY=0 NormalZ=1 AngleXU=0 Radius=1.55
  constraints (4):
    c: Diameter(g0) = 3.1
    c: Diameter(g1) = 3.1
    c: Diameter(g2) = 3.1
    c: Diameter(g3) = 3.1
FEATURE [PartDesign::Pocket] Pocket012
  BaseFeature = -> Pocket011
  Direction = (0,0,-1)
  Length = 5
  Length2 = 5
  Profile = -> Sketch014
  ReferenceAxis = -> Sketch014 [N_Axis]
  Type = 0
FEATURE [PartDesign::Body] Body003  label="BackplaneBlock001"
  Group = -> [Sketch010,Pad002,Sketch011,Pocket009,Sketch012,Sketch013,Pocket010,Pocket011,Sketch014,Pocket012]
  Origin = -> Origin003
  Placement = pos=(85,85,0) rot=(0,0,1;0rad)
  Tip = -> Pocket012
FEATURE [Sketcher::SketchObject] Sketch015
  ExternalGeometry = -> [Pocket008]
  FullyConstrained = true
  MapMode = 5
  Placement = pos=(0,-25,0) rot=(1,0,0;1.5708rad)
  Support = -> [Pocket008]
  sketch-geometry (2):
    g0: Circle CenterX=-20 CenterY=14 CenterZ=0 NormalX=0 NormalY=0 NormalZ=1 AngleXU=0 Radius=1.4
    g1: Circle CenterX=20 CenterY=14 CenterZ=0 NormalX=0 NormalY=0 NormalZ=1 AngleXU=0 Radius=1.4
  constraints (6):
    c: Diameter(g0) = 2.8
    c: Diameter(g1) = 2.8
    c: Distance(g0,g-5) = 5
    c: Distance(g0,g-3) = 6
    c: Distance(g1,g-3) = 6
    c: Distance(g1,g-4) = 5
FEATURE [PartDesign::Pocket] Pocket013
  BaseFeature = -> Pocket008
  Direction = (0,1,-2e-16)
  Length = 3
  Length2 = 5
  Profile = -> Sketch015
  ReferenceAxis = -> Sketch015 [N_Axis]
  Type = 0
FEATURE [Sketcher::SketchObject] Sketch016
  FullyConstrained = true
  MapMode = 5
  Support = -> [XY_Plane004]
  sketch-geometry (4):
    g0: LineSegment StartX=-25 StartY=25 StartZ=0 EndX=25 EndY=25 EndZ=0
    g1: LineSegment StartX=25 StartY=25 StartZ=0 EndX=25 EndY=-25 EndZ=0
    g2: LineSegment StartX=25 StartY=-25 StartZ=0 EndX=-25 EndY=-25 EndZ=0
    g3: LineSegment StartX=-25 StartY=-25 StartZ=0 EndX=-25 EndY=25 EndZ=0
  constraints (10):
    c: Coincident(g0,g1)
    c: Coincident(g1,g2)
    c: Coincident(g2,g3)
    c: Coincident(g3,g0)
    c: Horizontal(g0)
    c: Vertical(g3)
    c: Symmetric(g2,g1,g-2)
    c: Symmetric(g1,g0,g-1)
    c: DistanceY(g1,g1) = 50
    c: DistanceX(g2,g2) = 50
FEATURE [PartDesign::Pad] Pad003
  Direction = (0,0,1)
  Length = 20
  Length2 = 10
  Profile = -> Sketch016
  ReferenceAxis = -> Sketch016 [N_Axis]
  Type = 0
FEATURE [Sketcher::SketchObject] Sketch017
  ExternalGeometry = -> [Pad003]
  FullyConstrained = true
  MapMode = 5
  Placement = pos=(0,0,20) rot=(0,0,1;0rad)
  Support = -> [Pad003]
  sketch-geometry (36):
    g0: LineSegment StartX=-18 StartY=15 StartZ=0 EndX=-17 EndY=15 EndZ=0
    g1: LineSegment StartX=20 StartY=13 StartZ=0 EndX=20 EndY=-13 EndZ=0
    g2: LineSegment StartX=18 StartY=-15 StartZ=0 EndX=17 EndY=-15 EndZ=0
    g3: LineSegment StartX=-20 StartY=-13 StartZ=0 EndX=-20 EndY=13 EndZ=0
    g4: LineSegment StartX=-13 StartY=20 StartZ=0 EndX=13 EndY=20 EndZ=0
    g5: LineSegment StartX=15 StartY=18 StartZ=0 EndX=15 EndY=17 EndZ=0
    g6: LineSegment StartX=13 StartY=-20 StartZ=0 EndX=-13 EndY=-20 EndZ=0
    g7: LineSegment StartX=-15 StartY=-18 StartZ=0 EndX=-15 EndY=-17 EndZ=0
    g8: LineSegment StartX=17 StartY=15 StartZ=0 EndX=18 EndY=15 EndZ=0
    g9: LineSegment StartX=-15 StartY=17 StartZ=0 EndX=-15 EndY=18 EndZ=0
    g10: LineSegment StartX=-17 StartY=-15 StartZ=0 EndX=-18 EndY=-15 EndZ=0
    g11: LineSegment StartX=15 StartY=-17 StartZ=0 EndX=15 EndY=-18 EndZ=0
    g12: ArcOfCircle CenterX=-13 CenterY=-18 CenterZ=0 NormalX=0 NormalY=0 NormalZ=1 AngleXU=0 Radius=2 StartAngle=3.14159 EndAngle=4.71239
    g13: GeomPoint X=-15 Y=-20 Z=0
    g14: ArcOfCircle CenterX=13 CenterY=-18 CenterZ=0 NormalX=0 NormalY=0 NormalZ=1 AngleXU=0 Radius=2 StartAngle=4.71239 EndAngle=6.28319
    g15: GeomPoint X=15 Y=-20 Z=0
    g16: ArcOfCircle CenterX=17 CenterY=-17 CenterZ=0 NormalX=0 NormalY=0 NormalZ=1 AngleXU=0 Radius=2 StartAngle=1.5708 EndAngle=3.14159
    g17: GeomPoint X=15 Y=-15 Z=0
    g18: ArcOfCircle CenterX=18 CenterY=-13 CenterZ=0 NormalX=0 NormalY=0 NormalZ=1 AngleXU=0 Radius=2 StartAngle=4.71239 EndAngle=6.28319
    g19: GeomPoint X=20 Y=-15 Z=0
    g20: ArcOfCircle CenterX=18 CenterY=13 CenterZ=0 NormalX=0 NormalY=0 NormalZ=1 AngleXU=0 Radius=2 StartAngle=0 EndAngle=1.5708
    g21: GeomPoint X=20 Y=15 Z=0
    g22: ArcOfCircle CenterX=17 CenterY=17 CenterZ=0 NormalX=0 NormalY=0 NormalZ=1 AngleXU=0 Radius=2 StartAngle=3.14159 EndAngle=4.71239
    g23: GeomPoint X=15 Y=15 Z=0
    g24: ArcOfCircle CenterX=13 CenterY=18 CenterZ=0 NormalX=0 NormalY=0 NormalZ=1 AngleXU=0 Radius=2 StartAngle=4e-16 EndAngle=1.5708
    g25: GeomPoint X=15 Y=20 Z=0
    g26: ArcOfCircle CenterX=-13 CenterY=18 CenterZ=0 NormalX=0 NormalY=0 NormalZ=1 AngleXU=0 Radius=2 StartAngle=1.5708 EndAngle=3.14159
    g27: GeomPoint X=-15 Y=20 Z=0
    g28: ArcOfCircle CenterX=-17 CenterY=17 CenterZ=0 NormalX=0 NormalY=0 NormalZ=1 AngleXU=0 Radius=2 StartAngle=4.71239 EndAngle=6.28319
    g29: GeomPoint X=-15 Y=15 Z=0
    g30: ArcOfCircle CenterX=-18 CenterY=13 CenterZ=0 NormalX=0 NormalY=0 NormalZ=1 AngleXU=0 Radius=2 StartAngle=1.5708 EndAngle=3.14159
    g31: GeomPoint X=-20 Y=15 Z=0
    g32: ArcOfCircle CenterX=-18 CenterY=-13 CenterZ=0 NormalX=0 NormalY=0 NormalZ=1 AngleXU=0 Radius=2 StartAngle=3.14159 EndAngle=4.71239
    g33: GeomPoint X=-20 Y=-15 Z=0
    g34: ArcOfCircle CenterX=-17 CenterY=-17 CenterZ=0 NormalX=0 NormalY=0 NormalZ=1 AngleXU=0 Radius=2 StartAngle=0 EndAngle=1.5708
    g35: GeomPoint X=-15 Y=-15 Z=0
  constraints (80):
    c: Horizontal(g2)
    c: Vertical(g3)
    c: Symmetric(g21,g31,g-2)
    c: Symmetric(g21,g19,g-1)
    c: DistanceX(g31,g21) = 40
    c: DistanceY(g19,g21) = 30
    c: Horizontal(g4)
    c: Vertical(g7)
    c: Symmetric(g13,g15,g-2)
    c: Symmetric(g15,g25,g-1)
    c: DistanceY(g15,g25) = 40
    c: Vertical(g9)
    c: Vertical(g5)
    c: Vertical(g11)
    c: Horizontal(g10)
    c: Horizontal(g8)
    c: Horizontal(g0)
    c: DistanceX(g13,g15) = 30
    c: DistanceY(g33,g31) = 30
    c: DistanceX(g27,g25) = 30
    c: PointOnObject(g13,g7)
    c: PointOnObject(g13,g6)
    c: Tangent(g7,g12) = 1.5708
    c: Tangent(g6,g12) = 1.5708
    c: Radius(g12) = 2
    c: PointOnObject(g15,g11)
    c: PointOnObject(g15,g6)
    c: Tangent(g11,g14) = 1.5708
    c: Tangent(g6,g14) = 1.5708
    c: PointOnObject(g17,g11)
    c: PointOnObject(g17,g2)
    c: Tangent(g11,g16) = -1.5708
    c: Tangent(g2,g16) = -1.5708
    c: PointOnObject(g19,g2)
    c: PointOnObject(g19,g1)
    c: Tangent(g2,g18) = 1.5708
    c: Tangent(g1,g18) = 1.5708
    c: PointOnObject(g21,g1)
    c: PointOnObject(g21,g8)
    c: Tangent(g1,g20) = 1.5708
    c: Tangent(g8,g20) = 1.5708
    c: PointOnObject(g23,g8)
    c: PointOnObject(g23,g5)
    c: Tangent(g8,g22) = -1.5708
    c: Tangent(g5,g22) = -1.5708
    c: PointOnObject(g25,g5)
    c: PointOnObject(g25,g4)
    c: Tangent(g5,g24) = 1.5708
    c: Tangent(g4,g24) = 1.5708
    c: PointOnObject(g27,g9)
    c: PointOnObject(g27,g4)
    c: Tangent(g9,g26) = 1.5708
    c: Tangent(g4,g26) = 1.5708
    c: PointOnObject(g29,g9)
    c: PointOnObject(g29,g0)
    c: Tangent(g9,g28) = -1.5708
    c: Tangent(g0,g28) = -1.5708
    c: PointOnObject(g31,g0)
    c: PointOnObject(g31,g3)
    c: Tangent(g0,g30) = 1.5708
    c: Tangent(g3,g30) = 1.5708
    c: PointOnObject(g33,g3)
    c: PointOnObject(g33,g10)
    c: Tangent(g3,g32) = 1.5708
    c: Tangent(g10,g32) = 1.5708
    c: PointOnObject(g35,g10)
    c: PointOnObject(g35,g7)
    c: Tangent(g10,g34) = -1.5708
    c: Tangent(g7,g34) = -1.5708
    c: Radius(g34) = 2
    c: Radius(g32) = 2
    c: Radius(g30) = 2
    c: Radius(g28) = 2
    c: Radius(g26) = 2
    c: Radius(g24) = 2
    c: Radius(g22) = 2
    c: Radius(g20) = 2
    c: Radius(g18) = 2
    c: Radius(g16) = 2
    c: Radius(g14) = 2
FEATURE [PartDesign::Pocket] Pocket014
  BaseFeature = -> Pad003
  Direction = (0,0,-1)
  Length = 5
  Length2 = 5
  Profile = -> Sketch017
  ReferenceAxis = -> Sketch017 [N_Axis]
  Type = 1
FEATURE [Sketcher::SketchObject] Sketch018
  ExternalGeometry = -> [Pocket014]
  FullyConstrained = true
  MapMode = 5
  Placement = pos=(25,0,0) rot=(0.57735,0.57735,0.57735;2.0944rad)
  Support = -> [Pocket014]
  sketch-geometry (6):
    g0: LineSegment StartX=-15 StartY=10 StartZ=0 EndX=15 EndY=10 EndZ=0
    g1: LineSegment StartX=20 StartY=5 StartZ=0 EndX=20 EndY=0 EndZ=0
    g2: LineSegment StartX=20 StartY=0 StartZ=0 EndX=-20 EndY=0 EndZ=0
    g3: LineSegment StartX=-20 StartY=0 StartZ=0 EndX=-20 EndY=5 EndZ=0
    g4: ArcOfCircle CenterX=15 CenterY=5 CenterZ=0 NormalX=0 NormalY=0 NormalZ=1 AngleXU=0 Radius=5 StartAngle=1.11001e-11 EndAngle=1.5708
    g5: ArcOfCircle CenterX=-15 CenterY=5 CenterZ=0 NormalX=0 NormalY=0 NormalZ=1 AngleXU=0 Radius=5 StartAngle=1.5708 EndAngle=3.14159
  constraints (15):
    c: Coincident(g1,g2)
    c: Coincident(g2,g3)
    c: Vertical(g1)
    c: Vertical(g3)
    c: PointOnObject(g1,g-1)
    c: Tangent(g1,g4) = 1.5708
    c: Tangent(g0,g4) = 1.5708
    c: Tangent(g0,g5) = 1.5708
    c: Tangent(g3,g5) = 1.5708
    c: Horizontal(g0)
    c: DistanceX(g2,g2) = 40
    c: Symmetric(g2,g1,g-2)
    c: Distance(g-1,g0) = 10
    c: Radius(g5) = 5
    c: Radius(g4) = 5
FEATURE [PartDesign::Pocket] Pocket015
  BaseFeature = -> Pocket014
  Direction = (-1,0,0)
  Length = 5
  Length2 = 5
  Profile = -> Sketch018
  ReferenceAxis = -> Sketch018 [N_Axis]
  Type = 1
FEATURE [Sketcher::SketchObject] Sketch019
  FullyConstrained = true
  MapMode = 5
  Placement = pos=(0,-25,0) rot=(1,0,0;1.5708rad)
  Support = -> [Pocket014]
  sketch-geometry (6):
    g0: LineSegment StartX=-15 StartY=10 StartZ=0 EndX=15 EndY=10 EndZ=0
    g1: LineSegment StartX=20 StartY=5 StartZ=0 EndX=20 EndY=0 EndZ=0
    g2: LineSegment StartX=20 StartY=0 StartZ=0 EndX=-20 EndY=0 EndZ=0
    g3: LineSegment StartX=-20 StartY=0 StartZ=0 EndX=-20 EndY=5 EndZ=0
    g4: ArcOfCircle CenterX=15 CenterY=5 CenterZ=0 NormalX=0 NormalY=0 NormalZ=1 AngleXU=0 Radius=5 StartAngle=1.11e-11 EndAngle=1.5708
    g5: ArcOfCircle CenterX=-15 CenterY=5 CenterZ=0 NormalX=0 NormalY=0 NormalZ=1 AngleXU=0 Radius=5 StartAngle=1.5708 EndAngle=3.14159
  constraints (15):
    c: Coincident(g1,g2)
    c: Coincident(g2,g3)
    c: Horizontal(g0)
    c: Vertical(g1)
    c: Vertical(g3)
    c: Symmetric(g2,g1,g-2)
    c: PointOnObject(g1,g-1)
    c: Tangent(g0,g4) = 1.5708
    c: Tangent(g1,g4) = 1.5708
    c: Tangent(g0,g5) = 1.5708
    c: Tangent(g3,g5) = 1.5708
    c: DistanceX(g2,g2) = 40
    c: Distance(g-1,g0) = 10
    c: Radius(g5) = 5
    c: Radius(g4) = 5
FEATURE [PartDesign::Pocket] Pocket016
  BaseFeature = -> Pocket015
  Direction = (0,1,-2e-16)
  Length = 5
  Length2 = 5
  Profile = -> Sketch019
  ReferenceAxis = -> Sketch019 [N_Axis]
  Type = 1
FEATURE [Sketcher::SketchObject] Sketch020
  FullyConstrained = false
  MapMode = 5
  Placement = pos=(0,0,20) rot=(0,0,1;0rad)
  sketch-geometry (4):
    g0: Circle CenterX=-20 CenterY=20 CenterZ=0 NormalX=0 NormalY=0 NormalZ=1 AngleXU=0 Radius=1.55
    g1: Circle CenterX=20 CenterY=20 CenterZ=0 NormalX=0 NormalY=0 NormalZ=1 AngleXU=0 Radius=1.55
    g2: Circle CenterX=20 CenterY=-20 CenterZ=0 NormalX=0 NormalY=0 NormalZ=1 AngleXU=0 Radius=1.55
    g3: Circle CenterX=-20 CenterY=-20 CenterZ=0 NormalX=0 NormalY=0 NormalZ=1 AngleXU=0 Radius=1.55
  constraints (4):
    c: Diameter(g0) = 3.1
    c: Diameter(g1) = 3.1
    c: Diameter(g2) = 3.1
    c: Diameter(g3) = 3.1
FEATURE [PartDesign::Pocket] Pocket017
  BaseFeature = -> Pocket016
  Direction = (0,0,-1)
  Length = 5
  Length2 = 5
  Profile = -> Sketch020
  ReferenceAxis = -> Sketch020 [N_Axis]
  Type = 0
FEATURE [Sketcher::SketchObject] Sketch021
  ExternalGeometry = -> [Pocket017]
  FullyConstrained = true
  MapMode = 5
  Placement = pos=(0,-25,0) rot=(1,0,0;1.5708rad)
  Support = -> [Pocket017]
  sketch-geometry (2):
    g0: Circle CenterX=-20 CenterY=14 CenterZ=0 NormalX=0 NormalY=0 NormalZ=1 AngleXU=0 Radius=1.4
    g1: Circle CenterX=20 CenterY=14 CenterZ=0 NormalX=0 NormalY=0 NormalZ=1 AngleXU=0 Radius=1.4
  constraints (6):
    c: Diameter(g0) = 2.8
    c: Diameter(g1) = 2.8
    c: Distance(g0,g-5) = 5
    c: Distance(g0,g-3) = 6
    c: Distance(g1,g-3) = 6
    c: Distance(g1,g-4) = 5
FEATURE [PartDesign::Pocket] Pocket018
  BaseFeature = -> Pocket017
  Direction = (0,1,-2e-16)
  Length = 3
  Length2 = 5
  Profile = -> Sketch021
  ReferenceAxis = -> Sketch021 [N_Axis]
  Type = 0
FEATURE [PartDesign::Body] Body004  label="BackplaneBlock002"
  Group = -> [Sketch016,Pad003,Sketch017,Pocket014,Sketch018,Sketch019,Pocket015,Pocket016,Sketch020,Pocket017,Sketch021,Pocket018]
  Origin = -> Origin004
  Placement = pos=(85,145,0) rot=(0,0,1;3.14159rad)
  Tip = -> Pocket018
FEATURE [Sketcher::SketchObject] Sketch022
  FullyConstrained = true
  MapMode = 5
  Support = -> [XY_Plane005]
  sketch-geometry (4):
    g0: LineSegment StartX=-25 StartY=25 StartZ=0 EndX=25 EndY=25 EndZ=0
    g1: LineSegment StartX=25 StartY=25 StartZ=0 EndX=25 EndY=-25 EndZ=0
    g2: LineSegment StartX=25 StartY=-25 StartZ=0 EndX=-25 EndY=-25 EndZ=0
    g3: LineSegment StartX=-25 StartY=-25 StartZ=0 EndX=-25 EndY=25 EndZ=0
  constraints (10):
    c: Coincident(g0,g1)
    c: Coincident(g1,g2)
    c: Coincident(g2,g3)
    c: Coincident(g3,g0)
    c: Horizontal(g0)
    c: Vertical(g3)
    c: Symmetric(g2,g1,g-2)
    c: Symmetric(g1,g0,g-1)
    c: DistanceY(g1,g1) = 50
    c: DistanceX(g2,g2) = 50
FEATURE [PartDesign::Pad] Pad004
  Direction = (0,0,1)
  Length = 20
  Length2 = 10
  Profile = -> Sketch022
  ReferenceAxis = -> Sketch022 [N_Axis]
  Type = 0
FEATURE [Sketcher::SketchObject] Sketch023
  ExternalGeometry = -> [Pad004]
  FullyConstrained = true
  MapMode = 5
  Placement = pos=(0,0,20) rot=(0,0,1;0rad)
  Support = -> [Pad004]
  sketch-geometry (36):
    g0: LineSegment StartX=-18 StartY=15 StartZ=0 EndX=-17 EndY=15 EndZ=0
    g1: LineSegment StartX=20 StartY=13 StartZ=0 EndX=20 EndY=-13 EndZ=0
    g2: LineSegment StartX=18 StartY=-15 StartZ=0 EndX=17 EndY=-15 EndZ=0
    g3: LineSegment StartX=-20 StartY=-13 StartZ=0 EndX=-20 EndY=13 EndZ=0
    g4: LineSegment StartX=-13 StartY=20 StartZ=0 EndX=13 EndY=20 EndZ=0
    g5: LineSegment StartX=15 StartY=18 StartZ=0 EndX=15 EndY=17 EndZ=0
    g6: LineSegment StartX=13 StartY=-20 StartZ=0 EndX=-13 EndY=-20 EndZ=0
    g7: LineSegment StartX=-15 StartY=-18 StartZ=0 EndX=-15 EndY=-17 EndZ=0
    g8: LineSegment StartX=17 StartY=15 StartZ=0 EndX=18 EndY=15 EndZ=0
    g9: LineSegment StartX=-15 StartY=17 StartZ=0 EndX=-15 EndY=18 EndZ=0
    g10: LineSegment StartX=-17 StartY=-15 StartZ=0 EndX=-18 EndY=-15 EndZ=0
    g11: LineSegment StartX=15 StartY=-17 StartZ=0 EndX=15 EndY=-18 EndZ=0
    g12: ArcOfCircle CenterX=-13 CenterY=-18 CenterZ=0 NormalX=0 NormalY=0 NormalZ=1 AngleXU=0 Radius=2 StartAngle=3.14159 EndAngle=4.71239
    g13: GeomPoint X=-15 Y=-20 Z=0
    g14: ArcOfCircle CenterX=13 CenterY=-18 CenterZ=0 NormalX=0 NormalY=0 NormalZ=1 AngleXU=0 Radius=2 StartAngle=4.71239 EndAngle=6.28319
    g15: GeomPoint X=15 Y=-20 Z=0
    g16: ArcOfCircle CenterX=17 CenterY=-17 CenterZ=0 NormalX=0 NormalY=0 NormalZ=1 AngleXU=0 Radius=2 StartAngle=1.5708 EndAngle=3.14159
    g17: GeomPoint X=15 Y=-15 Z=0
    g18: ArcOfCircle CenterX=18 CenterY=-13 CenterZ=0 NormalX=0 NormalY=0 NormalZ=1 AngleXU=0 Radius=2 StartAngle=4.71239 EndAngle=6.28319
    g19: GeomPoint X=20 Y=-15 Z=0
    g20: ArcOfCircle CenterX=18 CenterY=13 CenterZ=0 NormalX=0 NormalY=0 NormalZ=1 AngleXU=0 Radius=2 StartAngle=0 EndAngle=1.5708
    g21: GeomPoint X=20 Y=15 Z=0
    g22: ArcOfCircle CenterX=17 CenterY=17 CenterZ=0 NormalX=0 NormalY=0 NormalZ=1 AngleXU=0 Radius=2 StartAngle=3.14159 EndAngle=4.71239
    g23: GeomPoint X=15 Y=15 Z=0
    g24: ArcOfCircle CenterX=13 CenterY=18 CenterZ=0 NormalX=0 NormalY=0 NormalZ=1 AngleXU=0 Radius=2 StartAngle=4e-16 EndAngle=1.5708
    g25: GeomPoint X=15 Y=20 Z=0
    g26: ArcOfCircle CenterX=-13 CenterY=18 CenterZ=0 NormalX=0 NormalY=0 NormalZ=1 AngleXU=0 Radius=2 StartAngle=1.5708 EndAngle=3.14159
    g27: GeomPoint X=-15 Y=20 Z=0
    g28: ArcOfCircle CenterX=-17 CenterY=17 CenterZ=0 NormalX=0 NormalY=0 NormalZ=1 AngleXU=0 Radius=2 StartAngle=4.71239 EndAngle=6.28319
    g29: GeomPoint X=-15 Y=15 Z=0
    g30: ArcOfCircle CenterX=-18 CenterY=13 CenterZ=0 NormalX=0 NormalY=0 NormalZ=1 AngleXU=0 Radius=2 StartAngle=1.5708 EndAngle=3.14159
    g31: GeomPoint X=-20 Y=15 Z=0
    g32: ArcOfCircle CenterX=-18 CenterY=-13 CenterZ=0 NormalX=0 NormalY=0 NormalZ=1 AngleXU=0 Radius=2 StartAngle=3.14159 EndAngle=4.71239
    g33: GeomPoint X=-20 Y=-15 Z=0
    g34: ArcOfCircle CenterX=-17 CenterY=-17 CenterZ=0 NormalX=0 NormalY=0 NormalZ=1 AngleXU=0 Radius=2 StartAngle=0 EndAngle=1.5708
    g35: GeomPoint X=-15 Y=-15 Z=0
  constraints (80):
    c: Horizontal(g2)
    c: Vertical(g3)
    c: Symmetric(g21,g31,g-2)
    c: Symmetric(g21,g19,g-1)
    c: DistanceX(g31,g21) = 40
    c: DistanceY(g19,g21) = 30
    c: Horizontal(g4)
    c: Vertical(g7)
    c: Symmetric(g13,g15,g-2)
    c: Symmetric(g15,g25,g-1)
    c: DistanceY(g15,g25) = 40
    c: Vertical(g9)
    c: Vertical(g5)
    c: Vertical(g11)
    c: Horizontal(g10)
    c: Horizontal(g8)
    c: Horizontal(g0)
    c: DistanceX(g13,g15) = 30
    c: DistanceY(g33,g31) = 30
    c: DistanceX(g27,g25) = 30
    c: PointOnObject(g13,g7)
    c: PointOnObject(g13,g6)
    c: Tangent(g7,g12) = 1.5708
    c: Tangent(g6,g12) = 1.5708
    c: Radius(g12) = 2
    c: PointOnObject(g15,g11)
    c: PointOnObject(g15,g6)
    c: Tangent(g11,g14) = 1.5708
    c: Tangent(g6,g14) = 1.5708
    c: PointOnObject(g17,g11)
    c: PointOnObject(g17,g2)
    c: Tangent(g11,g16) = -1.5708
    c: Tangent(g2,g16) = -1.5708
    c: PointOnObject(g19,g2)
    c: PointOnObject(g19,g1)
    c: Tangent(g2,g18) = 1.5708
    c: Tangent(g1,g18) = 1.5708
    c: PointOnObject(g21,g1)
    c: PointOnObject(g21,g8)
    c: Tangent(g1,g20) = 1.5708
    c: Tangent(g8,g20) = 1.5708
    c: PointOnObject(g23,g8)
    c: PointOnObject(g23,g5)
    c: Tangent(g8,g22) = -1.5708
    c: Tangent(g5,g22) = -1.5708
    c: PointOnObject(g25,g5)
    c: PointOnObject(g25,g4)
    c: Tangent(g5,g24) = 1.5708
    c: Tangent(g4,g24) = 1.5708
    c: PointOnObject(g27,g9)
    c: PointOnObject(g27,g4)
    c: Tangent(g9,g26) = 1.5708
    c: Tangent(g4,g26) = 1.5708
    c: PointOnObject(g29,g9)
    c: PointOnObject(g29,g0)
    c: Tangent(g9,g28) = -1.5708
    c: Tangent(g0,g28) = -1.5708
    c: PointOnObject(g31,g0)
    c: PointOnObject(g31,g3)
    c: Tangent(g0,g30) = 1.5708
    c: Tangent(g3,g30) = 1.5708
    c: PointOnObject(g33,g3)
    c: PointOnObject(g33,g10)
    c: Tangent(g3,g32) = 1.5708
    c: Tangent(g10,g32) = 1.5708
    c: PointOnObject(g35,g10)
    c: PointOnObject(g35,g7)
    c: Tangent(g10,g34) = -1.5708
    c: Tangent(g7,g34) = -1.5708
    c: Radius(g34) = 2
    c: Radius(g32) = 2
    c: Radius(g30) = 2
    c: Radius(g28) = 2
    c: Radius(g26) = 2
    c: Radius(g24) = 2
    c: Radius(g22) = 2
    c: Radius(g20) = 2
    c: Radius(g18) = 2
    c: Radius(g16) = 2
    c: Radius(g14) = 2
FEATURE [PartDesign::Pocket] Pocket019
  BaseFeature = -> Pad004
  Direction = (0,0,-1)
  Length = 5
  Length2 = 5
  Profile = -> Sketch023
  ReferenceAxis = -> Sketch023 [N_Axis]
  Type = 1
FEATURE [Sketcher::SketchObject] Sketch024
  ExternalGeometry = -> [Pocket019]
  FullyConstrained = true
  MapMode = 5
  Placement = pos=(25,0,0) rot=(0.57735,0.57735,0.57735;2.0944rad)
  Support = -> [Pocket019]
  sketch-geometry (6):
    g0: LineSegment StartX=-15 StartY=10 StartZ=0 EndX=15 EndY=10 EndZ=0
    g1: LineSegment StartX=20 StartY=5 StartZ=0 EndX=20 EndY=0 EndZ=0
    g2: LineSegment StartX=20 StartY=0 StartZ=0 EndX=-20 EndY=0 EndZ=0
    g3: LineSegment StartX=-20 StartY=0 StartZ=0 EndX=-20 EndY=5 EndZ=0
    g4: ArcOfCircle CenterX=15 CenterY=5 CenterZ=0 NormalX=0 NormalY=0 NormalZ=1 AngleXU=0 Radius=5 StartAngle=1.11001e-11 EndAngle=1.5708
    g5: ArcOfCircle CenterX=-15 CenterY=5 CenterZ=0 NormalX=0 NormalY=0 NormalZ=1 AngleXU=0 Radius=5 StartAngle=1.5708 EndAngle=3.14159
  constraints (15):
    c: Coincident(g1,g2)
    c: Coincident(g2,g3)
    c: Vertical(g1)
    c: Vertical(g3)
    c: PointOnObject(g1,g-1)
    c: Tangent(g1,g4) = 1.5708
    c: Tangent(g0,g4) = 1.5708
    c: Tangent(g0,g5) = 1.5708
    c: Tangent(g3,g5) = 1.5708
    c: Horizontal(g0)
    c: DistanceX(g2,g2) = 40
    c: Symmetric(g2,g1,g-2)
    c: Distance(g-1,g0) = 10
    c: Radius(g5) = 5
    c: Radius(g4) = 5
FEATURE [PartDesign::Pocket] Pocket020
  BaseFeature = -> Pocket019
  Direction = (-1,0,0)
  Length = 5
  Length2 = 5
  Profile = -> Sketch024
  ReferenceAxis = -> Sketch024 [N_Axis]
  Type = 1
FEATURE [Sketcher::SketchObject] Sketch025
  FullyConstrained = true
  MapMode = 5
  Placement = pos=(0,-25,0) rot=(1,0,0;1.5708rad)
  Support = -> [Pocket019]
  sketch-geometry (6):
    g0: LineSegment StartX=-15 StartY=10 StartZ=0 EndX=15 EndY=10 EndZ=0
    g1: LineSegment StartX=20 StartY=5 StartZ=0 EndX=20 EndY=0 EndZ=0
    g2: LineSegment StartX=20 StartY=0 StartZ=0 EndX=-20 EndY=0 EndZ=0
    g3: LineSegment StartX=-20 StartY=0 StartZ=0 EndX=-20 EndY=5 EndZ=0
    g4: ArcOfCircle CenterX=15 CenterY=5 CenterZ=0 NormalX=0 NormalY=0 NormalZ=1 AngleXU=0 Radius=5 StartAngle=1.11e-11 EndAngle=1.5708
    g5: ArcOfCircle CenterX=-15 CenterY=5 CenterZ=0 NormalX=0 NormalY=0 NormalZ=1 AngleXU=0 Radius=5 StartAngle=1.5708 EndAngle=3.14159
  constraints (15):
    c: Coincident(g1,g2)
    c: Coincident(g2,g3)
    c: Horizontal(g0)
    c: Vertical(g1)
    c: Vertical(g3)
    c: Symmetric(g2,g1,g-2)
    c: PointOnObject(g1,g-1)
    c: Tangent(g0,g4) = 1.5708
    c: Tangent(g1,g4) = 1.5708
    c: Tangent(g0,g5) = 1.5708
    c: Tangent(g3,g5) = 1.5708
    c: DistanceX(g2,g2) = 40
    c: Distance(g-1,g0) = 10
    c: Radius(g5) = 5
    c: Radius(g4) = 5
FEATURE [PartDesign::Pocket] Pocket021
  BaseFeature = -> Pocket020
  Direction = (0,1,-2e-16)
  Length = 5
  Length2 = 5
  Profile = -> Sketch025
  ReferenceAxis = -> Sketch025 [N_Axis]
  Type = 1
FEATURE [Sketcher::SketchObject] Sketch026
  FullyConstrained = false
  MapMode = 5
  Placement = pos=(0,0,20) rot=(0,0,1;0rad)
  sketch-geometry (4):
    g0: Circle CenterX=-20 CenterY=20 CenterZ=0 NormalX=0 NormalY=0 NormalZ=1 AngleXU=0 Radius=1.55
    g1: Circle CenterX=20 CenterY=20 CenterZ=0 NormalX=0 NormalY=0 NormalZ=1 AngleXU=0 Radius=1.55
    g2: Circle CenterX=20 CenterY=-20 CenterZ=0 NormalX=0 NormalY=0 NormalZ=1 AngleXU=0 Radius=1.55
    g3: Circle CenterX=-20 CenterY=-20 CenterZ=0 NormalX=0 NormalY=0 NormalZ=1 AngleXU=0 Radius=1.55
  constraints (4):
    c: Diameter(g0) = 3.1
    c: Diameter(g1) = 3.1
    c: Diameter(g2) = 3.1
    c: Diameter(g3) = 3.1
FEATURE [PartDesign::Pocket] Pocket022
  BaseFeature = -> Pocket021
  Direction = (0,0,-1)
  Length = 5
  Length2 = 5
  Profile = -> Sketch026
  ReferenceAxis = -> Sketch026 [N_Axis]
  Type = 0
FEATURE [Sketcher::SketchObject] Sketch027
  ExternalGeometry = -> [Pocket022]
  FullyConstrained = true
  MapMode = 5
  Placement = pos=(0,-25,0) rot=(1,0,0;1.5708rad)
  Support = -> [Pocket022]
  sketch-geometry (2):
    g0: Circle CenterX=-20 CenterY=14 CenterZ=0 NormalX=0 NormalY=0 NormalZ=1 AngleXU=0 Radius=1.4
    g1: Circle CenterX=20 CenterY=14 CenterZ=0 NormalX=0 NormalY=0 NormalZ=1 AngleXU=0 Radius=1.4
  constraints (6):
    c: Diameter(g0) = 2.8
    c: Diameter(g1) = 2.8
    c: Distance(g0,g-5) = 5
    c: Distance(g0,g-3) = 6
    c: Distance(g1,g-3) = 6
    c: Distance(g1,g-4) = 5
FEATURE [PartDesign::Pocket] Pocket023
  BaseFeature = -> Pocket022
  Direction = (0,1,-2e-16)
  Length = 3
  Length2 = 5
  Profile = -> Sketch027
  ReferenceAxis = -> Sketch027 [N_Axis]
  Type = 0
FEATURE [PartDesign::Body] Body005  label="BackplaneBlock003"
  Group = -> [Sketch022,Pad004,Sketch023,Pocket019,Sketch024,Sketch025,Pocket020,Pocket021,Sketch026,Pocket022,Sketch027,Pocket023]
  Origin = -> Origin005
  Placement = pos=(25,85,0) rot=(0,0,-1;1.5708rad)
  Tip = -> Pocket023
FEATURE [Sketcher::SketchObject] Sketch028
  FullyConstrained = true
  MapMode = 5
  Support = -> [XY_Plane006]
  sketch-geometry (4):
    g0: LineSegment StartX=-25 StartY=25 StartZ=0 EndX=25 EndY=25 EndZ=0
    g1: LineSegment StartX=25 StartY=25 StartZ=0 EndX=25 EndY=-25 EndZ=0
    g2: LineSegment StartX=25 StartY=-25 StartZ=0 EndX=-25 EndY=-25 EndZ=0
    g3: LineSegment StartX=-25 StartY=-25 StartZ=0 EndX=-25 EndY=25 EndZ=0
  constraints (10):
    c: Coincident(g0,g1)
    c: Coincident(g1,g2)
    c: Coincident(g2,g3)
    c: Coincident(g3,g0)
    c: Horizontal(g0)
    c: Vertical(g3)
    c: Symmetric(g2,g1,g-2)
    c: Symmetric(g1,g0,g-1)
    c: DistanceY(g1,g1) = 50
    c: DistanceX(g2,g2) = 50
FEATURE [PartDesign::Pad] Pad005
  Direction = (0,0,1)
  Length = 20
  Length2 = 10
  Profile = -> Sketch028
  ReferenceAxis = -> Sketch028 [N_Axis]
  Type = 0
FEATURE [Sketcher::SketchObject] Sketch029
  ExternalGeometry = -> [Pad005]
  FullyConstrained = true
  MapMode = 5
  Placement = pos=(0,0,20) rot=(0,0,1;0rad)
  Support = -> [Pad005]
  sketch-geometry (36):
    g0: LineSegment StartX=-18 StartY=15 StartZ=0 EndX=-17 EndY=15 EndZ=0
    g1: LineSegment StartX=20 StartY=13 StartZ=0 EndX=20 EndY=-13 EndZ=0
    g2: LineSegment StartX=18 StartY=-15 StartZ=0 EndX=17 EndY=-15 EndZ=0
    g3: LineSegment StartX=-20 StartY=-13 StartZ=0 EndX=-20 EndY=13 EndZ=0
    g4: LineSegment StartX=-13 StartY=20 StartZ=0 EndX=13 EndY=20 EndZ=0
    g5: LineSegment StartX=15 StartY=18 StartZ=0 EndX=15 EndY=17 EndZ=0
    g6: LineSegment StartX=13 StartY=-20 StartZ=0 EndX=-13 EndY=-20 EndZ=0
    g7: LineSegment StartX=-15 StartY=-18 StartZ=0 EndX=-15 EndY=-17 EndZ=0
    g8: LineSegment StartX=17 StartY=15 StartZ=0 EndX=18 EndY=15 EndZ=0
    g9: LineSegment StartX=-15 StartY=17 StartZ=0 EndX=-15 EndY=18 EndZ=0
    g10: LineSegment StartX=-17 StartY=-15 StartZ=0 EndX=-18 EndY=-15 EndZ=0
    g11: LineSegment StartX=15 StartY=-17 StartZ=0 EndX=15 EndY=-18 EndZ=0
    g12: ArcOfCircle CenterX=-13 CenterY=-18 CenterZ=0 NormalX=0 NormalY=0 NormalZ=1 AngleXU=0 Radius=2 StartAngle=3.14159 EndAngle=4.71239
    g13: GeomPoint X=-15 Y=-20 Z=0
    g14: ArcOfCircle CenterX=13 CenterY=-18 CenterZ=0 NormalX=0 NormalY=0 NormalZ=1 AngleXU=0 Radius=2 StartAngle=4.71239 EndAngle=6.28319
    g15: GeomPoint X=15 Y=-20 Z=0
    g16: ArcOfCircle CenterX=17 CenterY=-17 CenterZ=0 NormalX=0 NormalY=0 NormalZ=1 AngleXU=0 Radius=2 StartAngle=1.5708 EndAngle=3.14159
    g17: GeomPoint X=15 Y=-15 Z=0
    g18: ArcOfCircle CenterX=18 CenterY=-13 CenterZ=0 NormalX=0 NormalY=0 NormalZ=1 AngleXU=0 Radius=2 StartAngle=4.71239 EndAngle=6.28319
    g19: GeomPoint X=20 Y=-15 Z=0
    g20: ArcOfCircle CenterX=18 CenterY=13 CenterZ=0 NormalX=0 NormalY=0 NormalZ=1 AngleXU=0 Radius=2 StartAngle=0 EndAngle=1.5708
    g21: GeomPoint X=20 Y=15 Z=0
    g22: ArcOfCircle CenterX=17 CenterY=17 CenterZ=0 NormalX=0 NormalY=0 NormalZ=1 AngleXU=0 Radius=2 StartAngle=3.14159 EndAngle=4.71239
    g23: GeomPoint X=15 Y=15 Z=0
    g24: ArcOfCircle CenterX=13 CenterY=18 CenterZ=0 NormalX=0 NormalY=0 NormalZ=1 AngleXU=0 Radius=2 StartAngle=4e-16 EndAngle=1.5708
    g25: GeomPoint X=15 Y=20 Z=0
    g26: ArcOfCircle CenterX=-13 CenterY=18 CenterZ=0 NormalX=0 NormalY=0 NormalZ=1 AngleXU=0 Radius=2 StartAngle=1.5708 EndAngle=3.14159
    g27: GeomPoint X=-15 Y=20 Z=0
    g28: ArcOfCircle CenterX=-17 CenterY=17 CenterZ=0 NormalX=0 NormalY=0 NormalZ=1 AngleXU=0 Radius=2 StartAngle=4.71239 EndAngle=6.28319
    g29: GeomPoint X=-15 Y=15 Z=0
    g30: ArcOfCircle CenterX=-18 CenterY=13 CenterZ=0 NormalX=0 NormalY=0 NormalZ=1 AngleXU=0 Radius=2 StartAngle=1.5708 EndAngle=3.14159
    g31: GeomPoint X=-20 Y=15 Z=0
    g32: ArcOfCircle CenterX=-18 CenterY=-13 CenterZ=0 NormalX=0 NormalY=0 NormalZ=1 AngleXU=0 Radius=2 StartAngle=3.14159 EndAngle=4.71239
    g33: GeomPoint X=-20 Y=-15 Z=0
    g34: ArcOfCircle CenterX=-17 CenterY=-17 CenterZ=0 NormalX=0 NormalY=0 NormalZ=1 AngleXU=0 Radius=2 StartAngle=0 EndAngle=1.5708
    g35: GeomPoint X=-15 Y=-15 Z=0
  constraints (80):
    c: Horizontal(g2)
    c: Vertical(g3)
    c: Symmetric(g21,g31,g-2)
    c: Symmetric(g21,g19,g-1)
    c: DistanceX(g31,g21) = 40
    c: DistanceY(g19,g21) = 30
    c: Horizontal(g4)
    c: Vertical(g7)
    c: Symmetric(g13,g15,g-2)
    c: Symmetric(g15,g25,g-1)
    c: DistanceY(g15,g25) = 40
    c: Vertical(g9)
    c: Vertical(g5)
    c: Vertical(g11)
    c: Horizontal(g10)
    c: Horizontal(g8)
    c: Horizontal(g0)
    c: DistanceX(g13,g15) = 30
    c: DistanceY(g33,g31) = 30
    c: DistanceX(g27,g25) = 30
    c: PointOnObject(g13,g7)
    c: PointOnObject(g13,g6)
    c: Tangent(g7,g12) = 1.5708
    c: Tangent(g6,g12) = 1.5708
    c: Radius(g12) = 2
    c: PointOnObject(g15,g11)
    c: PointOnObject(g15,g6)
    c: Tangent(g11,g14) = 1.5708
    c: Tangent(g6,g14) = 1.5708
    c: PointOnObject(g17,g11)
    c: PointOnObject(g17,g2)
    c: Tangent(g11,g16) = -1.5708
    c: Tangent(g2,g16) = -1.5708
    c: PointOnObject(g19,g2)
    c: PointOnObject(g19,g1)
    c: Tangent(g2,g18) = 1.5708
    c: Tangent(g1,g18) = 1.5708
    c: PointOnObject(g21,g1)
    c: PointOnObject(g21,g8)
    c: Tangent(g1,g20) = 1.5708
    c: Tangent(g8,g20) = 1.5708
    c: PointOnObject(g23,g8)
    c: PointOnObject(g23,g5)
    c: Tangent(g8,g22) = -1.5708
    c: Tangent(g5,g22) = -1.5708
    c: PointOnObject(g25,g5)
    c: PointOnObject(g25,g4)
    c: Tangent(g5,g24) = 1.5708
    c: Tangent(g4,g24) = 1.5708
    c: PointOnObject(g27,g9)
    c: PointOnObject(g27,g4)
    c: Tangent(g9,g26) = 1.5708
    c: Tangent(g4,g26) = 1.5708
    c: PointOnObject(g29,g9)
    c: PointOnObject(g29,g0)
    c: Tangent(g9,g28) = -1.5708
    c: Tangent(g0,g28) = -1.5708
    c: PointOnObject(g31,g0)
    c: PointOnObject(g31,g3)
    c: Tangent(g0,g30) = 1.5708
    c: Tangent(g3,g30) = 1.5708
    c: PointOnObject(g33,g3)
    c: PointOnObject(g33,g10)
    c: Tangent(g3,g32) = 1.5708
    c: Tangent(g10,g32) = 1.5708
    c: PointOnObject(g35,g10)
    c: PointOnObject(g35,g7)
    c: Tangent(g10,g34) = -1.5708
    c: Tangent(g7,g34) = -1.5708
    c: Radius(g34) = 2
    c: Radius(g32) = 2
    c: Radius(g30) = 2
    c: Radius(g28) = 2
    c: Radius(g26) = 2
    c: Radius(g24) = 2
    c: Radius(g22) = 2
    c: Radius(g20) = 2
    c: Radius(g18) = 2
    c: Radius(g16) = 2
    c: Radius(g14) = 2
FEATURE [PartDesign::Pocket] Pocket024
  BaseFeature = -> Pad005
  Direction = (0,0,-1)
  Length = 5
  Length2 = 5
  Profile = -> Sketch029
  ReferenceAxis = -> Sketch029 [N_Axis]
  Type = 1
FEATURE [Sketcher::SketchObject] Sketch030
  ExternalGeometry = -> [Pocket024]
  FullyConstrained = true
  MapMode = 5
  Placement = pos=(25,0,0) rot=(0.57735,0.57735,0.57735;2.0944rad)
  Support = -> [Pocket024]
  sketch-geometry (6):
    g0: LineSegment StartX=-15 StartY=10 StartZ=0 EndX=15 EndY=10 EndZ=0
    g1: LineSegment StartX=20 StartY=5 StartZ=0 EndX=20 EndY=0 EndZ=0
    g2: LineSegment StartX=20 StartY=0 StartZ=0 EndX=-20 EndY=0 EndZ=0
    g3: LineSegment StartX=-20 StartY=0 StartZ=0 EndX=-20 EndY=5 EndZ=0
    g4: ArcOfCircle CenterX=15 CenterY=5 CenterZ=0 NormalX=0 NormalY=0 NormalZ=1 AngleXU=0 Radius=5 StartAngle=1.11001e-11 EndAngle=1.5708
    g5: ArcOfCircle CenterX=-15 CenterY=5 CenterZ=0 NormalX=0 NormalY=0 NormalZ=1 AngleXU=0 Radius=5 StartAngle=1.5708 EndAngle=3.14159
  constraints (15):
    c: Coincident(g1,g2)
    c: Coincident(g2,g3)
    c: Vertical(g1)
    c: Vertical(g3)
    c: PointOnObject(g1,g-1)
    c: Tangent(g1,g4) = 1.5708
    c: Tangent(g0,g4) = 1.5708
    c: Tangent(g0,g5) = 1.5708
    c: Tangent(g3,g5) = 1.5708
    c: Horizontal(g0)
    c: DistanceX(g2,g2) = 40
    c: Symmetric(g2,g1,g-2)
    c: Distance(g-1,g0) = 10
    c: Radius(g5) = 5
    c: Radius(g4) = 5
FEATURE [PartDesign::Pocket] Pocket025
  BaseFeature = -> Pocket024
  Direction = (-1,0,0)
  Length = 5
  Length2 = 5
  Profile = -> Sketch030
  ReferenceAxis = -> Sketch030 [N_Axis]
  Type = 1
FEATURE [Sketcher::SketchObject] Sketch031
  FullyConstrained = true
  MapMode = 5
  Placement = pos=(0,-25,0) rot=(1,0,0;1.5708rad)
  Support = -> [Pocket024]
  sketch-geometry (6):
    g0: LineSegment StartX=-15 StartY=10 StartZ=0 EndX=15 EndY=10 EndZ=0
    g1: LineSegment StartX=20 StartY=5 StartZ=0 EndX=20 EndY=0 EndZ=0
    g2: LineSegment StartX=20 StartY=0 StartZ=0 EndX=-20 EndY=0 EndZ=0
    g3: LineSegment StartX=-20 StartY=0 StartZ=0 EndX=-20 EndY=5 EndZ=0
    g4: ArcOfCircle CenterX=15 CenterY=5 CenterZ=0 NormalX=0 NormalY=0 NormalZ=1 AngleXU=0 Radius=5 StartAngle=1.11e-11 EndAngle=1.5708
    g5: ArcOfCircle CenterX=-15 CenterY=5 CenterZ=0 NormalX=0 NormalY=0 NormalZ=1 AngleXU=0 Radius=5 StartAngle=1.5708 EndAngle=3.14159
  constraints (15):
    c: Coincident(g1,g2)
    c: Coincident(g2,g3)
    c: Horizontal(g0)
    c: Vertical(g1)
    c: Vertical(g3)
    c: Symmetric(g2,g1,g-2)
    c: PointOnObject(g1,g-1)
    c: Tangent(g0,g4) = 1.5708
    c: Tangent(g1,g4) = 1.5708
    c: Tangent(g0,g5) = 1.5708
    c: Tangent(g3,g5) = 1.5708
    c: DistanceX(g2,g2) = 40
    c: Distance(g-1,g0) = 10
    c: Radius(g5) = 5
    c: Radius(g4) = 5
FEATURE [PartDesign::Pocket] Pocket026
  BaseFeature = -> Pocket025
  Direction = (0,1,-2e-16)
  Length = 5
  Length2 = 5
  Profile = -> Sketch031
  ReferenceAxis = -> Sketch031 [N_Axis]
  Type = 1
FEATURE [Sketcher::SketchObject] Sketch032
  FullyConstrained = false
  MapMode = 5
  Placement = pos=(0,0,20) rot=(0,0,1;0rad)
  sketch-geometry (4):
    g0: Circle CenterX=-20 CenterY=20 CenterZ=0 NormalX=0 NormalY=0 NormalZ=1 AngleXU=0 Radius=1.55
    g1: Circle CenterX=20 CenterY=20 CenterZ=0 NormalX=0 NormalY=0 NormalZ=1 AngleXU=0 Radius=1.55
    g2: Circle CenterX=20 CenterY=-20 CenterZ=0 NormalX=0 NormalY=0 NormalZ=1 AngleXU=0 Radius=1.55
    g3: Circle CenterX=-20 CenterY=-20 CenterZ=0 NormalX=0 NormalY=0 NormalZ=1 AngleXU=0 Radius=1.55
  constraints (4):
    c: Diameter(g0) = 3.1
    c: Diameter(g1) = 3.1
    c: Diameter(g2) = 3.1
    c: Diameter(g3) = 3.1
FEATURE [PartDesign::Pocket] Pocket027
  BaseFeature = -> Pocket026
  Direction = (0,0,-1)
  Length = 5
  Length2 = 5
  Profile = -> Sketch032
  ReferenceAxis = -> Sketch032 [N_Axis]
  Type = 0
FEATURE [Sketcher::SketchObject] Sketch033
  ExternalGeometry = -> [Pocket027]
  FullyConstrained = true
  MapMode = 5
  Placement = pos=(0,-25,0) rot=(1,0,0;1.5708rad)
  Support = -> [Pocket027]
  sketch-geometry (2):
    g0: Circle CenterX=-20 CenterY=14 CenterZ=0 NormalX=0 NormalY=0 NormalZ=1 AngleXU=0 Radius=1.4
    g1: Circle CenterX=20 CenterY=14 CenterZ=0 NormalX=0 NormalY=0 NormalZ=1 AngleXU=0 Radius=1.4
  constraints (6):
    c: Diameter(g0) = 2.8
    c: Diameter(g1) = 2.8
    c: Distance(g0,g-5) = 5
    c: Distance(g0,g-3) = 6
    c: Distance(g1,g-3) = 6
    c: Distance(g1,g-4) = 5
FEATURE [PartDesign::Pocket] Pocket028
  BaseFeature = -> Pocket027
  Direction = (0,1,-2e-16)
  Length = 3
  Length2 = 5
  Profile = -> Sketch033
  ReferenceAxis = -> Sketch033 [N_Axis]
  Type = 0
FEATURE [PartDesign::Body] Body006  label="BackplaneBlock004"
  Group = -> [Sketch028,Pad005,Sketch029,Pocket024,Sketch030,Sketch031,Pocket025,Pocket026,Sketch032,Pocket027,Sketch033,Pocket028]
  Origin = -> Origin006
  Placement = pos=(145,85,0) rot=(0,0,1;1.5708rad)
  Tip = -> Pocket028
FEATURE [Sketcher::SketchObject] Sketch034
  FullyConstrained = true
  MapMode = 5
  Support = -> [XY_Plane007]
  sketch-geometry (4):
    g0: LineSegment StartX=-25 StartY=25 StartZ=0 EndX=25 EndY=25 EndZ=0
    g1: LineSegment StartX=25 StartY=25 StartZ=0 EndX=25 EndY=-25 EndZ=0
    g2: LineSegment StartX=25 StartY=-25 StartZ=0 EndX=-25 EndY=-25 EndZ=0
    g3: LineSegment StartX=-25 StartY=-25 StartZ=0 EndX=-25 EndY=25 EndZ=0
  constraints (10):
    c: Coincident(g0,g1)
    c: Coincident(g1,g2)
    c: Coincident(g2,g3)
    c: Coincident(g3,g0)
    c: Horizontal(g0)
    c: Vertical(g3)
    c: Symmetric(g2,g1,g-2)
    c: Symmetric(g1,g0,g-1)
    c: DistanceY(g1,g1) = 50
    c: DistanceX(g2,g2) = 50
FEATURE [PartDesign::Pad] Pad006
  Direction = (0,0,1)
  Length = 20
  Length2 = 10
  Profile = -> Sketch034
  ReferenceAxis = -> Sketch034 [N_Axis]
  Type = 0
FEATURE [Sketcher::SketchObject] Sketch035
  ExternalGeometry = -> [Pad006]
  FullyConstrained = true
  MapMode = 5
  Placement = pos=(0,0,20) rot=(0,0,1;0rad)
  Support = -> [Pad006]
  sketch-geometry (36):
    g0: LineSegment StartX=-18 StartY=15 StartZ=0 EndX=-17 EndY=15 EndZ=0
    g1: LineSegment StartX=20 StartY=13 StartZ=0 EndX=20 EndY=-13 EndZ=0
    g2: LineSegment StartX=18 StartY=-15 StartZ=0 EndX=17 EndY=-15 EndZ=0
    g3: LineSegment StartX=-20 StartY=-13 StartZ=0 EndX=-20 EndY=13 EndZ=0
    g4: LineSegment StartX=-13 StartY=20 StartZ=0 EndX=13 EndY=20 EndZ=0
    g5: LineSegment StartX=15 StartY=18 StartZ=0 EndX=15 EndY=17 EndZ=0
    g6: LineSegment StartX=13 StartY=-20 StartZ=0 EndX=-13 EndY=-20 EndZ=0
    g7: LineSegment StartX=-15 StartY=-18 StartZ=0 EndX=-15 EndY=-17 EndZ=0
    g8: LineSegment StartX=17 StartY=15 StartZ=0 EndX=18 EndY=15 EndZ=0
    g9: LineSegment StartX=-15 StartY=17 StartZ=0 EndX=-15 EndY=18 EndZ=0
    g10: LineSegment StartX=-17 StartY=-15 StartZ=0 EndX=-18 EndY=-15 EndZ=0
    g11: LineSegment StartX=15 StartY=-17 StartZ=0 EndX=15 EndY=-18 EndZ=0
    g12: ArcOfCircle CenterX=-13 CenterY=-18 CenterZ=0 NormalX=0 NormalY=0 NormalZ=1 AngleXU=0 Radius=2 StartAngle=3.14159 EndAngle=4.71239
    g13: GeomPoint X=-15 Y=-20 Z=0
    g14: ArcOfCircle CenterX=13 CenterY=-18 CenterZ=0 NormalX=0 NormalY=0 NormalZ=1 AngleXU=0 Radius=2 StartAngle=4.71239 EndAngle=6.28319
    g15: GeomPoint X=15 Y=-20 Z=0
    g16: ArcOfCircle CenterX=17 CenterY=-17 CenterZ=0 NormalX=0 NormalY=0 NormalZ=1 AngleXU=0 Radius=2 StartAngle=1.5708 EndAngle=3.14159
    g17: GeomPoint X=15 Y=-15 Z=0
    g18: ArcOfCircle CenterX=18 CenterY=-13 CenterZ=0 NormalX=0 NormalY=0 NormalZ=1 AngleXU=0 Radius=2 StartAngle=4.71239 EndAngle=6.28319
    g19: GeomPoint X=20 Y=-15 Z=0
    g20: ArcOfCircle CenterX=18 CenterY=13 CenterZ=0 NormalX=0 NormalY=0 NormalZ=1 AngleXU=0 Radius=2 StartAngle=0 EndAngle=1.5708
    g21: GeomPoint X=20 Y=15 Z=0
    g22: ArcOfCircle CenterX=17 CenterY=17 CenterZ=0 NormalX=0 NormalY=0 NormalZ=1 AngleXU=0 Radius=2 StartAngle=3.14159 EndAngle=4.71239
    g23: GeomPoint X=15 Y=15 Z=0
    g24: ArcOfCircle CenterX=13 CenterY=18 CenterZ=0 NormalX=0 NormalY=0 NormalZ=1 AngleXU=0 Radius=2 StartAngle=4e-16 EndAngle=1.5708
    g25: GeomPoint X=15 Y=20 Z=0
    g26: ArcOfCircle CenterX=-13 CenterY=18 CenterZ=0 NormalX=0 NormalY=0 NormalZ=1 AngleXU=0 Radius=2 StartAngle=1.5708 EndAngle=3.14159
    g27: GeomPoint X=-15 Y=20 Z=0
    g28: ArcOfCircle CenterX=-17 CenterY=17 CenterZ=0 NormalX=0 NormalY=0 NormalZ=1 AngleXU=0 Radius=2 StartAngle=4.71239 EndAngle=6.28319
    g29: GeomPoint X=-15 Y=15 Z=0
    g30: ArcOfCircle CenterX=-18 CenterY=13 CenterZ=0 NormalX=0 NormalY=0 NormalZ=1 AngleXU=0 Radius=2 StartAngle=1.5708 EndAngle=3.14159
    g31: GeomPoint X=-20 Y=15 Z=0
    g32: ArcOfCircle CenterX=-18 CenterY=-13 CenterZ=0 NormalX=0 NormalY=0 NormalZ=1 AngleXU=0 Radius=2 StartAngle=3.14159 EndAngle=4.71239
    g33: GeomPoint X=-20 Y=-15 Z=0
    g34: ArcOfCircle CenterX=-17 CenterY=-17 CenterZ=0 NormalX=0 NormalY=0 NormalZ=1 AngleXU=0 Radius=2 StartAngle=0 EndAngle=1.5708
    g35: GeomPoint X=-15 Y=-15 Z=0
  constraints (80):
    c: Horizontal(g2)
    c: Vertical(g3)
    c: Symmetric(g21,g31,g-2)
    c: Symmetric(g21,g19,g-1)
    c: DistanceX(g31,g21) = 40
    c: DistanceY(g19,g21) = 30
    c: Horizontal(g4)
    c: Vertical(g7)
    c: Symmetric(g13,g15,g-2)
    c: Symmetric(g15,g25,g-1)
    c: DistanceY(g15,g25) = 40
    c: Vertical(g9)
    c: Vertical(g5)
    c: Vertical(g11)
    c: Horizontal(g10)
    c: Horizontal(g8)
    c: Horizontal(g0)
    c: DistanceX(g13,g15) = 30
    c: DistanceY(g33,g31) = 30
    c: DistanceX(g27,g25) = 30
    c: PointOnObject(g13,g7)
    c: PointOnObject(g13,g6)
    c: Tangent(g7,g12) = 1.5708
    c: Tangent(g6,g12) = 1.5708
    c: Radius(g12) = 2
    c: PointOnObject(g15,g11)
    c: PointOnObject(g15,g6)
    c: Tangent(g11,g14) = 1.5708
    c: Tangent(g6,g14) = 1.5708
    c: PointOnObject(g17,g11)
    c: PointOnObject(g17,g2)
    c: Tangent(g11,g16) = -1.5708
    c: Tangent(g2,g16) = -1.5708
    c: PointOnObject(g19,g2)
    c: PointOnObject(g19,g1)
    c: Tangent(g2,g18) = 1.5708
    c: Tangent(g1,g18) = 1.5708
    c: PointOnObject(g21,g1)
    c: PointOnObject(g21,g8)
    c: Tangent(g1,g20) = 1.5708
    c: Tangent(g8,g20) = 1.5708
    c: PointOnObject(g23,g8)
    c: PointOnObject(g23,g5)
    c: Tangent(g8,g22) = -1.5708
    c: Tangent(g5,g22) = -1.5708
    c: PointOnObject(g25,g5)
    c: PointOnObject(g25,g4)
    c: Tangent(g5,g24) = 1.5708
    c: Tangent(g4,g24) = 1.5708
    c: PointOnObject(g27,g9)
    c: PointOnObject(g27,g4)
    c: Tangent(g9,g26) = 1.5708
    c: Tangent(g4,g26) = 1.5708
    c: PointOnObject(g29,g9)
    c: PointOnObject(g29,g0)
    c: Tangent(g9,g28) = -1.5708
    c: Tangent(g0,g28) = -1.5708
    c: PointOnObject(g31,g0)
    c: PointOnObject(g31,g3)
    c: Tangent(g0,g30) = 1.5708
    c: Tangent(g3,g30) = 1.5708
    c: PointOnObject(g33,g3)
    c: PointOnObject(g33,g10)
    c: Tangent(g3,g32) = 1.5708
    c: Tangent(g10,g32) = 1.5708
    c: PointOnObject(g35,g10)
    c: PointOnObject(g35,g7)
    c: Tangent(g10,g34) = -1.5708
    c: Tangent(g7,g34) = -1.5708
    c: Radius(g34) = 2
    c: Radius(g32) = 2
    c: Radius(g30) = 2
    c: Radius(g28) = 2
    c: Radius(g26) = 2
    c: Radius(g24) = 2
    c: Radius(g22) = 2
    c: Radius(g20) = 2
    c: Radius(g18) = 2
    c: Radius(g16) = 2
    c: Radius(g14) = 2
FEATURE [PartDesign::Pocket] Pocket029
  BaseFeature = -> Pad006
  Direction = (0,0,-1)
  Length = 5
  Length2 = 5
  Profile = -> Sketch035
  ReferenceAxis = -> Sketch035 [N_Axis]
  Type = 1
FEATURE [Sketcher::SketchObject] Sketch036
  ExternalGeometry = -> [Pocket029]
  FullyConstrained = true
  MapMode = 5
  Placement = pos=(25,0,0) rot=(0.57735,0.57735,0.57735;2.0944rad)
  Support = -> [Pocket029]
  sketch-geometry (6):
    g0: LineSegment StartX=-15 StartY=10 StartZ=0 EndX=15 EndY=10 EndZ=0
    g1: LineSegment StartX=20 StartY=5 StartZ=0 EndX=20 EndY=0 EndZ=0
    g2: LineSegment StartX=20 StartY=0 StartZ=0 EndX=-20 EndY=0 EndZ=0
    g3: LineSegment StartX=-20 StartY=0 StartZ=0 EndX=-20 EndY=5 EndZ=0
    g4: ArcOfCircle CenterX=15 CenterY=5 CenterZ=0 NormalX=0 NormalY=0 NormalZ=1 AngleXU=0 Radius=5 StartAngle=1.11001e-11 EndAngle=1.5708
    g5: ArcOfCircle CenterX=-15 CenterY=5 CenterZ=0 NormalX=0 NormalY=0 NormalZ=1 AngleXU=0 Radius=5 StartAngle=1.5708 EndAngle=3.14159
  constraints (15):
    c: Coincident(g1,g2)
    c: Coincident(g2,g3)
    c: Vertical(g1)
    c: Vertical(g3)
    c: PointOnObject(g1,g-1)
    c: Tangent(g1,g4) = 1.5708
    c: Tangent(g0,g4) = 1.5708
    c: Tangent(g0,g5) = 1.5708
    c: Tangent(g3,g5) = 1.5708
    c: Horizontal(g0)
    c: DistanceX(g2,g2) = 40
    c: Symmetric(g2,g1,g-2)
    c: Distance(g-1,g0) = 10
    c: Radius(g5) = 5
    c: Radius(g4) = 5
FEATURE [PartDesign::Pocket] Pocket030
  BaseFeature = -> Pocket029
  Direction = (-1,0,0)
  Length = 5
  Length2 = 5
  Profile = -> Sketch036
  ReferenceAxis = -> Sketch036 [N_Axis]
  Type = 1
FEATURE [Sketcher::SketchObject] Sketch037
  FullyConstrained = true
  MapMode = 5
  Placement = pos=(0,-25,0) rot=(1,0,0;1.5708rad)
  Support = -> [Pocket029]
  sketch-geometry (6):
    g0: LineSegment StartX=-15 StartY=10 StartZ=0 EndX=15 EndY=10 EndZ=0
    g1: LineSegment StartX=20 StartY=5 StartZ=0 EndX=20 EndY=0 EndZ=0
    g2: LineSegment StartX=20 StartY=0 StartZ=0 EndX=-20 EndY=0 EndZ=0
    g3: LineSegment StartX=-20 StartY=0 StartZ=0 EndX=-20 EndY=5 EndZ=0
    g4: ArcOfCircle CenterX=15 CenterY=5 CenterZ=0 NormalX=0 NormalY=0 NormalZ=1 AngleXU=0 Radius=5 StartAngle=1.11e-11 EndAngle=1.5708
    g5: ArcOfCircle CenterX=-15 CenterY=5 CenterZ=0 NormalX=0 NormalY=0 NormalZ=1 AngleXU=0 Radius=5 StartAngle=1.5708 EndAngle=3.14159
  constraints (15):
    c: Coincident(g1,g2)
    c: Coincident(g2,g3)
    c: Horizontal(g0)
    c: Vertical(g1)
    c: Vertical(g3)
    c: Symmetric(g2,g1,g-2)
    c: PointOnObject(g1,g-1)
    c: Tangent(g0,g4) = 1.5708
    c: Tangent(g1,g4) = 1.5708
    c: Tangent(g0,g5) = 1.5708
    c: Tangent(g3,g5) = 1.5708
    c: DistanceX(g2,g2) = 40
    c: Distance(g-1,g0) = 10
    c: Radius(g5) = 5
    c: Radius(g4) = 5
FEATURE [PartDesign::Pocket] Pocket031
  BaseFeature = -> Pocket030
  Direction = (0,1,-2e-16)
  Length = 5
  Length2 = 5
  Profile = -> Sketch037
  ReferenceAxis = -> Sketch037 [N_Axis]
  Type = 1
FEATURE [Sketcher::SketchObject] Sketch038
  FullyConstrained = false
  MapMode = 5
  Placement = pos=(0,0,20) rot=(0,0,1;0rad)
  sketch-geometry (4):
    g0: Circle CenterX=-20 CenterY=20 CenterZ=0 NormalX=0 NormalY=0 NormalZ=1 AngleXU=0 Radius=1.55
    g1: Circle CenterX=20 CenterY=20 CenterZ=0 NormalX=0 NormalY=0 NormalZ=1 AngleXU=0 Radius=1.55
    g2: Circle CenterX=20 CenterY=-20 CenterZ=0 NormalX=0 NormalY=0 NormalZ=1 AngleXU=0 Radius=1.55
    g3: Circle CenterX=-20 CenterY=-20 CenterZ=0 NormalX=0 NormalY=0 NormalZ=1 AngleXU=0 Radius=1.55
  constraints (4):
    c: Diameter(g0) = 3.1
    c: Diameter(g1) = 3.1
    c: Diameter(g2) = 3.1
    c: Diameter(g3) = 3.1
FEATURE [PartDesign::Pocket] Pocket032
  BaseFeature = -> Pocket031
  Direction = (0,0,-1)
  Length = 5
  Length2 = 5
  Profile = -> Sketch038
  ReferenceAxis = -> Sketch038 [N_Axis]
  Type = 0
FEATURE [Sketcher::SketchObject] Sketch039
  ExternalGeometry = -> [Pocket032]
  FullyConstrained = true
  MapMode = 5
  Placement = pos=(0,-25,0) rot=(1,0,0;1.5708rad)
  Support = -> [Pocket032]
  sketch-geometry (2):
    g0: Circle CenterX=-20 CenterY=14 CenterZ=0 NormalX=0 NormalY=0 NormalZ=1 AngleXU=0 Radius=1.4
    g1: Circle CenterX=20 CenterY=14 CenterZ=0 NormalX=0 NormalY=0 NormalZ=1 AngleXU=0 Radius=1.4
  constraints (6):
    c: Diameter(g0) = 2.8
    c: Diameter(g1) = 2.8
    c: Distance(g0,g-5) = 5
    c: Distance(g0,g-3) = 6
    c: Distance(g1,g-3) = 6
    c: Distance(g1,g-4) = 5
FEATURE [PartDesign::Pocket] Pocket033
  BaseFeature = -> Pocket032
  Direction = (0,1,-2e-16)
  Length = 3
  Length2 = 5
  Profile = -> Sketch039
  ReferenceAxis = -> Sketch039 [N_Axis]
  Type = 0
FEATURE [PartDesign::Body] Body007  label="BackplaneBlock005"
  Group = -> [Sketch034,Pad006,Sketch035,Pocket029,Sketch036,Sketch037,Pocket030,Pocket031,Sketch038,Pocket032,Sketch039,Pocket033]
  Origin = -> Origin007
  Placement = pos=(85,25,0) rot=(0,0,1;0rad)
  Tip = -> Pocket033
FEATURE [Sketcher::SketchObject] Sketch040
  ExternalGeometry = -> [Pocket013]
  FullyConstrained = true
  MapMode = 5
  Placement = pos=(-25,0,0) rot=(0.57735,-0.57735,-0.57735;2.0944rad)
  Support = -> [Pocket013]
  sketch-geometry (2):
    g0: Circle CenterX=-20 CenterY=14 CenterZ=0 NormalX=0 NormalY=0 NormalZ=1 AngleXU=0 Radius=1.4
    g1: Circle CenterX=20 CenterY=14 CenterZ=0 NormalX=0 NormalY=0 NormalZ=1 AngleXU=0 Radius=1.4
  constraints (6):
    c: Diameter(g0) = 2.8
    c: Diameter(g1) = 2.8
    c: Distance(g0,g-3) = 5
    c: Distance(g0,g-4) = 6
    c: Distance(g1,g-4) = 6
    c: Distance(g1,g-5) = 5
FEATURE [PartDesign::Pocket] Pocket034
  BaseFeature = -> Pocket013
  Direction = (1,0,0)
  Length = 3
  Length2 = 5
  Profile = -> Sketch040
  ReferenceAxis = -> Sketch040 [N_Axis]
  Type = 0
FEATURE [PartDesign::Body] Body002  label="BackplaneBlock"
  Group = -> [Sketch002,Pad001,Sketch003,Pocket001,Sketch004,Sketch005,Pocket002,Pocket003,Sketch009,Pocket008,Sketch015,Pocket013,Sketch040,Pocket034]
  Origin = -> Origin002
  Placement = pos=(25,25,0) rot=(0,0,1;0rad)
  Tip = -> Pocket034
FEATURE [Sketcher::SketchObject] Sketch041
  FullyConstrained = true
  MapMode = 5
  Support = -> [XY_Plane008]
  sketch-geometry (4):
    g0: LineSegment StartX=-25 StartY=25 StartZ=0 EndX=25 EndY=25 EndZ=0
    g1: LineSegment StartX=25 StartY=25 StartZ=0 EndX=25 EndY=-25 EndZ=0
    g2: LineSegment StartX=25 StartY=-25 StartZ=0 EndX=-25 EndY=-25 EndZ=0
    g3: LineSegment StartX=-25 StartY=-25 StartZ=0 EndX=-25 EndY=25 EndZ=0
  constraints (10):
    c: Coincident(g0,g1)
    c: Coincident(g1,g2)
    c: Coincident(g2,g3)
    c: Coincident(g3,g0)
    c: Horizontal(g0)
    c: Vertical(g3)
    c: Symmetric(g2,g1,g-2)
    c: Symmetric(g1,g0,g-1)
    c: DistanceY(g1,g1) = 50
    c: DistanceX(g2,g2) = 50
FEATURE [PartDesign::Pad] Pad007
  Direction = (0,0,1)
  Length = 20
  Length2 = 10
  Profile = -> Sketch041
  ReferenceAxis = -> Sketch041 [N_Axis]
  Type = 0
FEATURE [Sketcher::SketchObject] Sketch042
  ExternalGeometry = -> [Pad007]
  FullyConstrained = true
  MapMode = 5
  Placement = pos=(0,0,20) rot=(0,0,1;0rad)
  Support = -> [Pad007]
  sketch-geometry (36):
    g0: LineSegment StartX=-18 StartY=15 StartZ=0 EndX=-17 EndY=15 EndZ=0
    g1: LineSegment StartX=20 StartY=13 StartZ=0 EndX=20 EndY=-13 EndZ=0
    g2: LineSegment StartX=18 StartY=-15 StartZ=0 EndX=17 EndY=-15 EndZ=0
    g3: LineSegment StartX=-20 StartY=-13 StartZ=0 EndX=-20 EndY=13 EndZ=0
    g4: LineSegment StartX=-13 StartY=20 StartZ=0 EndX=13 EndY=20 EndZ=0
    g5: LineSegment StartX=15 StartY=18 StartZ=0 EndX=15 EndY=17 EndZ=0
    g6: LineSegment StartX=13 StartY=-20 StartZ=0 EndX=-13 EndY=-20 EndZ=0
    g7: LineSegment StartX=-15 StartY=-18 StartZ=0 EndX=-15 EndY=-17 EndZ=0
    g8: LineSegment StartX=17 StartY=15 StartZ=0 EndX=18 EndY=15 EndZ=0
    g9: LineSegment StartX=-15 StartY=17 StartZ=0 EndX=-15 EndY=18 EndZ=0
    g10: LineSegment StartX=-17 StartY=-15 StartZ=0 EndX=-18 EndY=-15 EndZ=0
    g11: LineSegment StartX=15 StartY=-17 StartZ=0 EndX=15 EndY=-18 EndZ=0
    g12: ArcOfCircle CenterX=-13 CenterY=-18 CenterZ=0 NormalX=0 NormalY=0 NormalZ=1 AngleXU=0 Radius=2 StartAngle=3.14159 EndAngle=4.71239
    g13: GeomPoint X=-15 Y=-20 Z=0
    g14: ArcOfCircle CenterX=13 CenterY=-18 CenterZ=0 NormalX=0 NormalY=0 NormalZ=1 AngleXU=0 Radius=2 StartAngle=4.71239 EndAngle=6.28319
    g15: GeomPoint X=15 Y=-20 Z=0
    g16: ArcOfCircle CenterX=17 CenterY=-17 CenterZ=0 NormalX=0 NormalY=0 NormalZ=1 AngleXU=0 Radius=2 StartAngle=1.5708 EndAngle=3.14159
    g17: GeomPoint X=15 Y=-15 Z=0
    g18: ArcOfCircle CenterX=18 CenterY=-13 CenterZ=0 NormalX=0 NormalY=0 NormalZ=1 AngleXU=0 Radius=2 StartAngle=4.71239 EndAngle=6.28319
    g19: GeomPoint X=20 Y=-15 Z=0
    g20: ArcOfCircle CenterX=18 CenterY=13 CenterZ=0 NormalX=0 NormalY=0 NormalZ=1 AngleXU=0 Radius=2 StartAngle=0 EndAngle=1.5708
    g21: GeomPoint X=20 Y=15 Z=0
    g22: ArcOfCircle CenterX=17 CenterY=17 CenterZ=0 NormalX=0 NormalY=0 NormalZ=1 AngleXU=0 Radius=2 StartAngle=3.14159 EndAngle=4.71239
    g23: GeomPoint X=15 Y=15 Z=0
    g24: ArcOfCircle CenterX=13 CenterY=18 CenterZ=0 NormalX=0 NormalY=0 NormalZ=1 AngleXU=0 Radius=2 StartAngle=4e-16 EndAngle=1.5708
    g25: GeomPoint X=15 Y=20 Z=0
    g26: ArcOfCircle CenterX=-13 CenterY=18 CenterZ=0 NormalX=0 NormalY=0 NormalZ=1 AngleXU=0 Radius=2 StartAngle=1.5708 EndAngle=3.14159
    g27: GeomPoint X=-15 Y=20 Z=0
    g28: ArcOfCircle CenterX=-17 CenterY=17 CenterZ=0 NormalX=0 NormalY=0 NormalZ=1 AngleXU=0 Radius=2 StartAngle=4.71239 EndAngle=6.28319
    g29: GeomPoint X=-15 Y=15 Z=0
    g30: ArcOfCircle CenterX=-18 CenterY=13 CenterZ=0 NormalX=0 NormalY=0 NormalZ=1 AngleXU=0 Radius=2 StartAngle=1.5708 EndAngle=3.14159
    g31: GeomPoint X=-20 Y=15 Z=0
    g32: ArcOfCircle CenterX=-18 CenterY=-13 CenterZ=0 NormalX=0 NormalY=0 NormalZ=1 AngleXU=0 Radius=2 StartAngle=3.14159 EndAngle=4.71239
    g33: GeomPoint X=-20 Y=-15 Z=0
    g34: ArcOfCircle CenterX=-17 CenterY=-17 CenterZ=0 NormalX=0 NormalY=0 NormalZ=1 AngleXU=0 Radius=2 StartAngle=0 EndAngle=1.5708
    g35: GeomPoint X=-15 Y=-15 Z=0
  constraints (80):
    c: Horizontal(g2)
    c: Vertical(g3)
    c: Symmetric(g21,g31,g-2)
    c: Symmetric(g21,g19,g-1)
    c: DistanceX(g31,g21) = 40
    c: DistanceY(g19,g21) = 30
    c: Horizontal(g4)
    c: Vertical(g7)
    c: Symmetric(g13,g15,g-2)
    c: Symmetric(g15,g25,g-1)
    c: DistanceY(g15,g25) = 40
    c: Vertical(g9)
    c: Vertical(g5)
    c: Vertical(g11)
    c: Horizontal(g10)
    c: Horizontal(g8)
    c: Horizontal(g0)
    c: DistanceX(g13,g15) = 30
    c: DistanceY(g33,g31) = 30
    c: DistanceX(g27,g25) = 30
    c: PointOnObject(g13,g7)
    c: PointOnObject(g13,g6)
    c: Tangent(g7,g12) = 1.5708
    c: Tangent(g6,g12) = 1.5708
    c: Radius(g12) = 2
    c: PointOnObject(g15,g11)
    c: PointOnObject(g15,g6)
    c: Tangent(g11,g14) = 1.5708
    c: Tangent(g6,g14) = 1.5708
    c: PointOnObject(g17,g11)
    c: PointOnObject(g17,g2)
    c: Tangent(g11,g16) = -1.5708
    c: Tangent(g2,g16) = -1.5708
    c: PointOnObject(g19,g2)
    c: PointOnObject(g19,g1)
    c: Tangent(g2,g18) = 1.5708
    c: Tangent(g1,g18) = 1.5708
    c: PointOnObject(g21,g1)
    c: PointOnObject(g21,g8)
    c: Tangent(g1,g20) = 1.5708
    c: Tangent(g8,g20) = 1.5708
    c: PointOnObject(g23,g8)
    c: PointOnObject(g23,g5)
    c: Tangent(g8,g22) = -1.5708
    c: Tangent(g5,g22) = -1.5708
    c: PointOnObject(g25,g5)
    c: PointOnObject(g25,g4)
    c: Tangent(g5,g24) = 1.5708
    c: Tangent(g4,g24) = 1.5708
    c: PointOnObject(g27,g9)
    c: PointOnObject(g27,g4)
    c: Tangent(g9,g26) = 1.5708
    c: Tangent(g4,g26) = 1.5708
    c: PointOnObject(g29,g9)
    c: PointOnObject(g29,g0)
    c: Tangent(g9,g28) = -1.5708
    c: Tangent(g0,g28) = -1.5708
    c: PointOnObject(g31,g0)
    c: PointOnObject(g31,g3)
    c: Tangent(g0,g30) = 1.5708
    c: Tangent(g3,g30) = 1.5708
    c: PointOnObject(g33,g3)
    c: PointOnObject(g33,g10)
    c: Tangent(g3,g32) = 1.5708
    c: Tangent(g10,g32) = 1.5708
    c: PointOnObject(g35,g10)
    c: PointOnObject(g35,g7)
    c: Tangent(g10,g34) = -1.5708
    c: Tangent(g7,g34) = -1.5708
    c: Radius(g34) = 2
    c: Radius(g32) = 2
    c: Radius(g30) = 2
    c: Radius(g28) = 2
    c: Radius(g26) = 2
    c: Radius(g24) = 2
    c: Radius(g22) = 2
    c: Radius(g20) = 2
    c: Radius(g18) = 2
    c: Radius(g16) = 2
    c: Radius(g14) = 2
FEATURE [PartDesign::Pocket] Pocket035
  BaseFeature = -> Pad007
  Direction = (0,0,-1)
  Length = 5
  Length2 = 5
  Profile = -> Sketch042
  ReferenceAxis = -> Sketch042 [N_Axis]
  Type = 1
FEATURE [Sketcher::SketchObject] Sketch043
  ExternalGeometry = -> [Pocket035]
  FullyConstrained = true
  MapMode = 5
  Placement = pos=(25,0,0) rot=(0.57735,0.57735,0.57735;2.0944rad)
  Support = -> [Pocket035]
  sketch-geometry (6):
    g0: LineSegment StartX=-15 StartY=10 StartZ=0 EndX=15 EndY=10 EndZ=0
    g1: LineSegment StartX=20 StartY=5 StartZ=0 EndX=20 EndY=0 EndZ=0
    g2: LineSegment StartX=20 StartY=0 StartZ=0 EndX=-20 EndY=0 EndZ=0
    g3: LineSegment StartX=-20 StartY=0 StartZ=0 EndX=-20 EndY=5 EndZ=0
    g4: ArcOfCircle CenterX=15 CenterY=5 CenterZ=0 NormalX=0 NormalY=0 NormalZ=1 AngleXU=0 Radius=5 StartAngle=1.11001e-11 EndAngle=1.5708
    g5: ArcOfCircle CenterX=-15 CenterY=5 CenterZ=0 NormalX=0 NormalY=0 NormalZ=1 AngleXU=0 Radius=5 StartAngle=1.5708 EndAngle=3.14159
  constraints (15):
    c: Coincident(g1,g2)
    c: Coincident(g2,g3)
    c: Vertical(g1)
    c: Vertical(g3)
    c: PointOnObject(g1,g-1)
    c: Tangent(g1,g4) = 1.5708
    c: Tangent(g0,g4) = 1.5708
    c: Tangent(g0,g5) = 1.5708
    c: Tangent(g3,g5) = 1.5708
    c: Horizontal(g0)
    c: DistanceX(g2,g2) = 40
    c: Symmetric(g2,g1,g-2)
    c: Distance(g-1,g0) = 10
    c: Radius(g5) = 5
    c: Radius(g4) = 5
FEATURE [PartDesign::Pocket] Pocket036
  BaseFeature = -> Pocket035
  Direction = (-1,0,0)
  Length = 5
  Length2 = 5
  Profile = -> Sketch043
  ReferenceAxis = -> Sketch043 [N_Axis]
  Type = 1
FEATURE [Sketcher::SketchObject] Sketch044
  FullyConstrained = true
  MapMode = 5
  Placement = pos=(0,-25,0) rot=(1,0,0;1.5708rad)
  Support = -> [Pocket035]
  sketch-geometry (6):
    g0: LineSegment StartX=-15 StartY=10 StartZ=0 EndX=15 EndY=10 EndZ=0
    g1: LineSegment StartX=20 StartY=5 StartZ=0 EndX=20 EndY=0 EndZ=0
    g2: LineSegment StartX=20 StartY=0 StartZ=0 EndX=-20 EndY=0 EndZ=0
    g3: LineSegment StartX=-20 StartY=0 StartZ=0 EndX=-20 EndY=5 EndZ=0
    g4: ArcOfCircle CenterX=15 CenterY=5 CenterZ=0 NormalX=0 NormalY=0 NormalZ=1 AngleXU=0 Radius=5 StartAngle=1.11e-11 EndAngle=1.5708
    g5: ArcOfCircle CenterX=-15 CenterY=5 CenterZ=0 NormalX=0 NormalY=0 NormalZ=1 AngleXU=0 Radius=5 StartAngle=1.5708 EndAngle=3.14159
  constraints (15):
    c: Coincident(g1,g2)
    c: Coincident(g2,g3)
    c: Horizontal(g0)
    c: Vertical(g1)
    c: Vertical(g3)
    c: Symmetric(g2,g1,g-2)
    c: PointOnObject(g1,g-1)
    c: Tangent(g0,g4) = 1.5708
    c: Tangent(g1,g4) = 1.5708
    c: Tangent(g0,g5) = 1.5708
    c: Tangent(g3,g5) = 1.5708
    c: DistanceX(g2,g2) = 40
    c: Distance(g-1,g0) = 10
    c: Radius(g5) = 5
    c: Radius(g4) = 5
FEATURE [PartDesign::Pocket] Pocket037
  BaseFeature = -> Pocket036
  Direction = (0,1,-2e-16)
  Length = 5
  Length2 = 5
  Profile = -> Sketch044
  ReferenceAxis = -> Sketch044 [N_Axis]
  Type = 1
FEATURE [Sketcher::SketchObject] Sketch045
  FullyConstrained = false
  MapMode = 5
  Placement = pos=(0,0,20) rot=(0,0,1;0rad)
  sketch-geometry (4):
    g0: Circle CenterX=-20 CenterY=20 CenterZ=0 NormalX=0 NormalY=0 NormalZ=1 AngleXU=0 Radius=1.55
    g1: Circle CenterX=20 CenterY=20 CenterZ=0 NormalX=0 NormalY=0 NormalZ=1 AngleXU=0 Radius=1.55
    g2: Circle CenterX=20 CenterY=-20 CenterZ=0 NormalX=0 NormalY=0 NormalZ=1 AngleXU=0 Radius=1.55
    g3: Circle CenterX=-20 CenterY=-20 CenterZ=0 NormalX=0 NormalY=0 NormalZ=1 AngleXU=0 Radius=1.55
  constraints (4):
    c: Diameter(g0) = 3.1
    c: Diameter(g1) = 3.1
    c: Diameter(g2) = 3.1
    c: Diameter(g3) = 3.1
FEATURE [PartDesign::Pocket] Pocket038
  BaseFeature = -> Pocket037
  Direction = (0,0,-1)
  Length = 5
  Length2 = 5
  Profile = -> Sketch045
  ReferenceAxis = -> Sketch045 [N_Axis]
  Type = 0
FEATURE [Sketcher::SketchObject] Sketch046
  ExternalGeometry = -> [Pocket038]
  FullyConstrained = true
  MapMode = 5
  Placement = pos=(0,-25,0) rot=(1,0,0;1.5708rad)
  Support = -> [Pocket038]
  sketch-geometry (2):
    g0: Circle CenterX=-20 CenterY=14 CenterZ=0 NormalX=0 NormalY=0 NormalZ=1 AngleXU=0 Radius=1.55
    g1: Circle CenterX=20 CenterY=14 CenterZ=0 NormalX=0 NormalY=0 NormalZ=1 AngleXU=0 Radius=1.55
  constraints (6):
    c: Diameter(g0) = 3.1
    c: Diameter(g1) = 3.1
    c: Distance(g0,g-5) = 5
    c: Distance(g0,g-3) = 6
    c: Distance(g1,g-3) = 6
    c: Distance(g1,g-4) = 5
FEATURE [PartDesign::Pocket] Pocket039
  BaseFeature = -> Pocket038
  Direction = (0,1,-2e-16)
  Length = 3
  Length2 = 5
  Profile = -> Sketch046
  ReferenceAxis = -> Sketch046 [N_Axis]
  Type = 0
FEATURE [Sketcher::SketchObject] Sketch047
  ExternalGeometry = -> [Pocket039]
  FullyConstrained = true
  MapMode = 5
  Placement = pos=(-25,0,0) rot=(0.57735,-0.57735,-0.57735;2.0944rad)
  Support = -> [Pocket039]
  sketch-geometry (2):
    g0: Circle CenterX=-20 CenterY=14 CenterZ=0 NormalX=0 NormalY=0 NormalZ=1 AngleXU=0 Radius=1.4
    g1: Circle CenterX=20 CenterY=14 CenterZ=0 NormalX=0 NormalY=0 NormalZ=1 AngleXU=0 Radius=1.4
  constraints (6):
    c: Diameter(g0) = 2.8
    c: Diameter(g1) = 2.8
    c: Distance(g0,g-3) = 5
    c: Distance(g0,g-4) = 6
    c: Distance(g1,g-4) = 6
    c: Distance(g1,g-5) = 5
FEATURE [PartDesign::Pocket] Pocket040
  BaseFeature = -> Pocket039
  Direction = (1,0,0)
  Length = 3
  Length2 = 5
  Profile = -> Sketch047
  ReferenceAxis = -> Sketch047 [N_Axis]
  Type = 0
FEATURE [PartDesign::Body] Body008  label="BackplaneBlock006"
  Group = -> [Sketch041,Pad007,Sketch042,Pocket035,Sketch043,Sketch044,Pocket036,Pocket037,Sketch045,Pocket038,Sketch046,Pocket039,Sketch047,Pocket040]
  Origin = -> Origin008
  Placement = pos=(145,25,0) rot=(0,0,1;1.5708rad)
  Tip = -> Pocket040
FEATURE [Sketcher::SketchObject] Sketch048
  FullyConstrained = true
  MapMode = 5
  Support = -> [XY_Plane009]
  sketch-geometry (4):
    g0: LineSegment StartX=-25 StartY=25 StartZ=0 EndX=25 EndY=25 EndZ=0
    g1: LineSegment StartX=25 StartY=25 StartZ=0 EndX=25 EndY=-25 EndZ=0
    g2: LineSegment StartX=25 StartY=-25 StartZ=0 EndX=-25 EndY=-25 EndZ=0
    g3: LineSegment StartX=-25 StartY=-25 StartZ=0 EndX=-25 EndY=25 EndZ=0
  constraints (10):
    c: Coincident(g0,g1)
    c: Coincident(g1,g2)
    c: Coincident(g2,g3)
    c: Coincident(g3,g0)
    c: Horizontal(g0)
    c: Vertical(g3)
    c: Symmetric(g2,g1,g-2)
    c: Symmetric(g1,g0,g-1)
    c: DistanceY(g1,g1) = 50
    c: DistanceX(g2,g2) = 50
FEATURE [PartDesign::Pad] Pad008
  Direction = (0,0,1)
  Length = 20
  Length2 = 10
  Profile = -> Sketch048
  ReferenceAxis = -> Sketch048 [N_Axis]
  Type = 0
FEATURE [Sketcher::SketchObject] Sketch049
  ExternalGeometry = -> [Pad008]
  FullyConstrained = true
  MapMode = 5
  Placement = pos=(0,0,20) rot=(0,0,1;0rad)
  Support = -> [Pad008]
  sketch-geometry (36):
    g0: LineSegment StartX=-18 StartY=15 StartZ=0 EndX=-17 EndY=15 EndZ=0
    g1: LineSegment StartX=20 StartY=13 StartZ=0 EndX=20 EndY=-13 EndZ=0
    g2: LineSegment StartX=18 StartY=-15 StartZ=0 EndX=17 EndY=-15 EndZ=0
    g3: LineSegment StartX=-20 StartY=-13 StartZ=0 EndX=-20 EndY=13 EndZ=0
    g4: LineSegment StartX=-13 StartY=20 StartZ=0 EndX=13 EndY=20 EndZ=0
    g5: LineSegment StartX=15 StartY=18 StartZ=0 EndX=15 EndY=17 EndZ=0
    g6: LineSegment StartX=13 StartY=-20 StartZ=0 EndX=-13 EndY=-20 EndZ=0
    g7: LineSegment StartX=-15 StartY=-18 StartZ=0 EndX=-15 EndY=-17 EndZ=0
    g8: LineSegment StartX=17 StartY=15 StartZ=0 EndX=18 EndY=15 EndZ=0
    g9: LineSegment StartX=-15 StartY=17 StartZ=0 EndX=-15 EndY=18 EndZ=0
    g10: LineSegment StartX=-17 StartY=-15 StartZ=0 EndX=-18 EndY=-15 EndZ=0
    g11: LineSegment StartX=15 StartY=-17 StartZ=0 EndX=15 EndY=-18 EndZ=0
    g12: ArcOfCircle CenterX=-13 CenterY=-18 CenterZ=0 NormalX=0 NormalY=0 NormalZ=1 AngleXU=0 Radius=2 StartAngle=3.14159 EndAngle=4.71239
    g13: GeomPoint X=-15 Y=-20 Z=0
    g14: ArcOfCircle CenterX=13 CenterY=-18 CenterZ=0 NormalX=0 NormalY=0 NormalZ=1 AngleXU=0 Radius=2 StartAngle=4.71239 EndAngle=6.28319
    g15: GeomPoint X=15 Y=-20 Z=0
    g16: ArcOfCircle CenterX=17 CenterY=-17 CenterZ=0 NormalX=0 NormalY=0 NormalZ=1 AngleXU=0 Radius=2 StartAngle=1.5708 EndAngle=3.14159
    g17: GeomPoint X=15 Y=-15 Z=0
    g18: ArcOfCircle CenterX=18 CenterY=-13 CenterZ=0 NormalX=0 NormalY=0 NormalZ=1 AngleXU=0 Radius=2 StartAngle=4.71239 EndAngle=6.28319
    g19: GeomPoint X=20 Y=-15 Z=0
    g20: ArcOfCircle CenterX=18 CenterY=13 CenterZ=0 NormalX=0 NormalY=0 NormalZ=1 AngleXU=0 Radius=2 StartAngle=0 EndAngle=1.5708
    g21: GeomPoint X=20 Y=15 Z=0
    g22: ArcOfCircle CenterX=17 CenterY=17 CenterZ=0 NormalX=0 NormalY=0 NormalZ=1 AngleXU=0 Radius=2 StartAngle=3.14159 EndAngle=4.71239
    g23: GeomPoint X=15 Y=15 Z=0
    g24: ArcOfCircle CenterX=13 CenterY=18 CenterZ=0 NormalX=0 NormalY=0 NormalZ=1 AngleXU=0 Radius=2 StartAngle=4e-16 EndAngle=1.5708
    g25: GeomPoint X=15 Y=20 Z=0
    g26: ArcOfCircle CenterX=-13 CenterY=18 CenterZ=0 NormalX=0 NormalY=0 NormalZ=1 AngleXU=0 Radius=2 StartAngle=1.5708 EndAngle=3.14159
    g27: GeomPoint X=-15 Y=20 Z=0
    g28: ArcOfCircle CenterX=-17 CenterY=17 CenterZ=0 NormalX=0 NormalY=0 NormalZ=1 AngleXU=0 Radius=2 StartAngle=4.71239 EndAngle=6.28319
    g29: GeomPoint X=-15 Y=15 Z=0
    g30: ArcOfCircle CenterX=-18 CenterY=13 CenterZ=0 NormalX=0 NormalY=0 NormalZ=1 AngleXU=0 Radius=2 StartAngle=1.5708 EndAngle=3.14159
    g31: GeomPoint X=-20 Y=15 Z=0
    g32: ArcOfCircle CenterX=-18 CenterY=-13 CenterZ=0 NormalX=0 NormalY=0 NormalZ=1 AngleXU=0 Radius=2 StartAngle=3.14159 EndAngle=4.71239
    g33: GeomPoint X=-20 Y=-15 Z=0
    g34: ArcOfCircle CenterX=-17 CenterY=-17 CenterZ=0 NormalX=0 NormalY=0 NormalZ=1 AngleXU=0 Radius=2 StartAngle=0 EndAngle=1.5708
    g35: GeomPoint X=-15 Y=-15 Z=0
  constraints (80):
    c: Horizontal(g2)
    c: Vertical(g3)
    c: Symmetric(g21,g31,g-2)
    c: Symmetric(g21,g19,g-1)
    c: DistanceX(g31,g21) = 40
    c: DistanceY(g19,g21) = 30
    c: Horizontal(g4)
    c: Vertical(g7)
    c: Symmetric(g13,g15,g-2)
    c: Symmetric(g15,g25,g-1)
    c: DistanceY(g15,g25) = 40
    c: Vertical(g9)
    c: Vertical(g5)
    c: Vertical(g11)
    c: Horizontal(g10)
    c: Horizontal(g8)
    c: Horizontal(g0)
    c: DistanceX(g13,g15) = 30
    c: DistanceY(g33,g31) = 30
    c: DistanceX(g27,g25) = 30
    c: PointOnObject(g13,g7)
    c: PointOnObject(g13,g6)
    c: Tangent(g7,g12) = 1.5708
    c: Tangent(g6,g12) = 1.5708
    c: Radius(g12) = 2
    c: PointOnObject(g15,g11)
    c: PointOnObject(g15,g6)
    c: Tangent(g11,g14) = 1.5708
    c: Tangent(g6,g14) = 1.5708
    c: PointOnObject(g17,g11)
    c: PointOnObject(g17,g2)
    c: Tangent(g11,g16) = -1.5708
    c: Tangent(g2,g16) = -1.5708
    c: PointOnObject(g19,g2)
    c: PointOnObject(g19,g1)
    c: Tangent(g2,g18) = 1.5708
    c: Tangent(g1,g18) = 1.5708
    c: PointOnObject(g21,g1)
    c: PointOnObject(g21,g8)
    c: Tangent(g1,g20) = 1.5708
    c: Tangent(g8,g20) = 1.5708
    c: PointOnObject(g23,g8)
    c: PointOnObject(g23,g5)
    c: Tangent(g8,g22) = -1.5708
    c: Tangent(g5,g22) = -1.5708
    c: PointOnObject(g25,g5)
    c: PointOnObject(g25,g4)
    c: Tangent(g5,g24) = 1.5708
    c: Tangent(g4,g24) = 1.5708
    c: PointOnObject(g27,g9)
    c: PointOnObject(g27,g4)
    c: Tangent(g9,g26) = 1.5708
    c: Tangent(g4,g26) = 1.5708
    c: PointOnObject(g29,g9)
    c: PointOnObject(g29,g0)
    c: Tangent(g9,g28) = -1.5708
    c: Tangent(g0,g28) = -1.5708
    c: PointOnObject(g31,g0)
    c: PointOnObject(g31,g3)
    c: Tangent(g0,g30) = 1.5708
    c: Tangent(g3,g30) = 1.5708
    c: PointOnObject(g33,g3)
    c: PointOnObject(g33,g10)
    c: Tangent(g3,g32) = 1.5708
    c: Tangent(g10,g32) = 1.5708
    c: PointOnObject(g35,g10)
    c: PointOnObject(g35,g7)
    c: Tangent(g10,g34) = -1.5708
    c: Tangent(g7,g34) = -1.5708
    c: Radius(g34) = 2
    c: Radius(g32) = 2
    c: Radius(g30) = 2
    c: Radius(g28) = 2
    c: Radius(g26) = 2
    c: Radius(g24) = 2
    c: Radius(g22) = 2
    c: Radius(g20) = 2
    c: Radius(g18) = 2
    c: Radius(g16) = 2
    c: Radius(g14) = 2
FEATURE [PartDesign::Pocket] Pocket041
  BaseFeature = -> Pad008
  Direction = (0,0,-1)
  Length = 5
  Length2 = 5
  Profile = -> Sketch049
  ReferenceAxis = -> Sketch049 [N_Axis]
  Type = 1
FEATURE [Sketcher::SketchObject] Sketch050
  ExternalGeometry = -> [Pocket041]
  FullyConstrained = true
  MapMode = 5
  Placement = pos=(25,0,0) rot=(0.57735,0.57735,0.57735;2.0944rad)
  Support = -> [Pocket041]
  sketch-geometry (6):
    g0: LineSegment StartX=-15 StartY=10 StartZ=0 EndX=15 EndY=10 EndZ=0
    g1: LineSegment StartX=20 StartY=5 StartZ=0 EndX=20 EndY=0 EndZ=0
    g2: LineSegment StartX=20 StartY=0 StartZ=0 EndX=-20 EndY=0 EndZ=0
    g3: LineSegment StartX=-20 StartY=0 StartZ=0 EndX=-20 EndY=5 EndZ=0
    g4: ArcOfCircle CenterX=15 CenterY=5 CenterZ=0 NormalX=0 NormalY=0 NormalZ=1 AngleXU=0 Radius=5 StartAngle=1.11001e-11 EndAngle=1.5708
    g5: ArcOfCircle CenterX=-15 CenterY=5 CenterZ=0 NormalX=0 NormalY=0 NormalZ=1 AngleXU=0 Radius=5 StartAngle=1.5708 EndAngle=3.14159
  constraints (15):
    c: Coincident(g1,g2)
    c: Coincident(g2,g3)
    c: Vertical(g1)
    c: Vertical(g3)
    c: PointOnObject(g1,g-1)
    c: Tangent(g1,g4) = 1.5708
    c: Tangent(g0,g4) = 1.5708
    c: Tangent(g0,g5) = 1.5708
    c: Tangent(g3,g5) = 1.5708
    c: Horizontal(g0)
    c: DistanceX(g2,g2) = 40
    c: Symmetric(g2,g1,g-2)
    c: Distance(g-1,g0) = 10
    c: Radius(g5) = 5
    c: Radius(g4) = 5
FEATURE [PartDesign::Pocket] Pocket042
  BaseFeature = -> Pocket041
  Direction = (-1,0,0)
  Length = 5
  Length2 = 5
  Profile = -> Sketch050
  ReferenceAxis = -> Sketch050 [N_Axis]
  Type = 1
FEATURE [Sketcher::SketchObject] Sketch051
  FullyConstrained = true
  MapMode = 5
  Placement = pos=(0,-25,0) rot=(1,0,0;1.5708rad)
  Support = -> [Pocket041]
  sketch-geometry (6):
    g0: LineSegment StartX=-15 StartY=10 StartZ=0 EndX=15 EndY=10 EndZ=0
    g1: LineSegment StartX=20 StartY=5 StartZ=0 EndX=20 EndY=0 EndZ=0
    g2: LineSegment StartX=20 StartY=0 StartZ=0 EndX=-20 EndY=0 EndZ=0
    g3: LineSegment StartX=-20 StartY=0 StartZ=0 EndX=-20 EndY=5 EndZ=0
    g4: ArcOfCircle CenterX=15 CenterY=5 CenterZ=0 NormalX=0 NormalY=0 NormalZ=1 AngleXU=0 Radius=5 StartAngle=1.11e-11 EndAngle=1.5708
    g5: ArcOfCircle CenterX=-15 CenterY=5 CenterZ=0 NormalX=0 NormalY=0 NormalZ=1 AngleXU=0 Radius=5 StartAngle=1.5708 EndAngle=3.14159
  constraints (15):
    c: Coincident(g1,g2)
    c: Coincident(g2,g3)
    c: Horizontal(g0)
    c: Vertical(g1)
    c: Vertical(g3)
    c: Symmetric(g2,g1,g-2)
    c: PointOnObject(g1,g-1)
    c: Tangent(g0,g4) = 1.5708
    c: Tangent(g1,g4) = 1.5708
    c: Tangent(g0,g5) = 1.5708
    c: Tangent(g3,g5) = 1.5708
    c: DistanceX(g2,g2) = 40
    c: Distance(g-1,g0) = 10
    c: Radius(g5) = 5
    c: Radius(g4) = 5
FEATURE [PartDesign::Pocket] Pocket043
  BaseFeature = -> Pocket042
  Direction = (0,1,-2e-16)
  Length = 5
  Length2 = 5
  Profile = -> Sketch051
  ReferenceAxis = -> Sketch051 [N_Axis]
  Type = 1
FEATURE [Sketcher::SketchObject] Sketch052
  FullyConstrained = false
  MapMode = 5
  Placement = pos=(0,0,20) rot=(0,0,1;0rad)
  sketch-geometry (4):
    g0: Circle CenterX=-20 CenterY=20 CenterZ=0 NormalX=0 NormalY=0 NormalZ=1 AngleXU=0 Radius=1.55
    g1: Circle CenterX=20 CenterY=20 CenterZ=0 NormalX=0 NormalY=0 NormalZ=1 AngleXU=0 Radius=1.55
    g2: Circle CenterX=20 CenterY=-20 CenterZ=0 NormalX=0 NormalY=0 NormalZ=1 AngleXU=0 Radius=1.55
    g3: Circle CenterX=-20 CenterY=-20 CenterZ=0 NormalX=0 NormalY=0 NormalZ=1 AngleXU=0 Radius=1.55
  constraints (4):
    c: Diameter(g0) = 3.1
    c: Diameter(g1) = 3.1
    c: Diameter(g2) = 3.1
    c: Diameter(g3) = 3.1
FEATURE [PartDesign::Pocket] Pocket044
  BaseFeature = -> Pocket043
  Direction = (0,0,-1)
  Length = 5
  Length2 = 5
  Profile = -> Sketch052
  ReferenceAxis = -> Sketch052 [N_Axis]
  Type = 0
FEATURE [Sketcher::SketchObject] Sketch053
  ExternalGeometry = -> [Pocket044]
  FullyConstrained = true
  MapMode = 5
  Placement = pos=(0,-25,0) rot=(1,0,0;1.5708rad)
  Support = -> [Pocket044]
  sketch-geometry (2):
    g0: Circle CenterX=-20 CenterY=14 CenterZ=0 NormalX=0 NormalY=0 NormalZ=1 AngleXU=0 Radius=1.4
    g1: Circle CenterX=20 CenterY=14 CenterZ=0 NormalX=0 NormalY=0 NormalZ=1 AngleXU=0 Radius=1.4
  constraints (6):
    c: Diameter(g0) = 2.8
    c: Diameter(g1) = 2.8
    c: Distance(g0,g-5) = 5
    c: Distance(g0,g-3) = 6
    c: Distance(g1,g-3) = 6
    c: Distance(g1,g-4) = 5
FEATURE [PartDesign::Pocket] Pocket045
  BaseFeature = -> Pocket044
  Direction = (0,1,-2e-16)
  Length = 3
  Length2 = 5
  Profile = -> Sketch053
  ReferenceAxis = -> Sketch053 [N_Axis]
  Type = 0
FEATURE [Sketcher::SketchObject] Sketch054
  ExternalGeometry = -> [Pocket045]
  FullyConstrained = true
  MapMode = 5
  Placement = pos=(-25,0,0) rot=(0.57735,-0.57735,-0.57735;2.0944rad)
  Support = -> [Pocket045]
  sketch-geometry (2):
    g0: Circle CenterX=-20 CenterY=14 CenterZ=0 NormalX=0 NormalY=0 NormalZ=1 AngleXU=0 Radius=1.4
    g1: Circle CenterX=20 CenterY=14 CenterZ=0 NormalX=0 NormalY=0 NormalZ=1 AngleXU=0 Radius=1.4
  constraints (6):
    c: Diameter(g0) = 2.8
    c: Diameter(g1) = 2.8
    c: Distance(g0,g-3) = 5
    c: Distance(g0,g-4) = 6
    c: Distance(g1,g-4) = 6
    c: Distance(g1,g-5) = 5
FEATURE [PartDesign::Pocket] Pocket046
  BaseFeature = -> Pocket045
  Direction = (1,0,0)
  Length = 3
  Length2 = 5
  Profile = -> Sketch054
  ReferenceAxis = -> Sketch054 [N_Axis]
  Type = 0
FEATURE [PartDesign::Body] Body009  label="BackplaneBlock007"
  Group = -> [Sketch048,Pad008,Sketch049,Pocket041,Sketch050,Sketch051,Pocket042,Pocket043,Sketch052,Pocket044,Sketch053,Pocket045,Sketch054,Pocket046]
  Origin = -> Origin009
  Placement = pos=(25,145,0) rot=(0,0,-1;1.5708rad)
  Tip = -> Pocket046
FEATURE [Sketcher::SketchObject] Sketch055
  FullyConstrained = true
  MapMode = 5
  Support = -> [XY_Plane010]
  sketch-geometry (4):
    g0: LineSegment StartX=-25 StartY=25 StartZ=0 EndX=25 EndY=25 EndZ=0
    g1: LineSegment StartX=25 StartY=25 StartZ=0 EndX=25 EndY=-25 EndZ=0
    g2: LineSegment StartX=25 StartY=-25 StartZ=0 EndX=-25 EndY=-25 EndZ=0
    g3: LineSegment StartX=-25 StartY=-25 StartZ=0 EndX=-25 EndY=25 EndZ=0
  constraints (10):
    c: Coincident(g0,g1)
    c: Coincident(g1,g2)
    c: Coincident(g2,g3)
    c: Coincident(g3,g0)
    c: Horizontal(g0)
    c: Vertical(g3)
    c: Symmetric(g2,g1,g-2)
    c: Symmetric(g1,g0,g-1)
    c: DistanceY(g1,g1) = 50
    c: DistanceX(g2,g2) = 50
FEATURE [PartDesign::Pad] Pad009
  Direction = (0,0,1)
  Length = 20
  Length2 = 10
  Profile = -> Sketch055
  ReferenceAxis = -> Sketch055 [N_Axis]
  Type = 0
FEATURE [Sketcher::SketchObject] Sketch056
  ExternalGeometry = -> [Pad009]
  FullyConstrained = true
  MapMode = 5
  Placement = pos=(0,0,20) rot=(0,0,1;0rad)
  Support = -> [Pad009]
  sketch-geometry (36):
    g0: LineSegment StartX=-18 StartY=15 StartZ=0 EndX=-17 EndY=15 EndZ=0
    g1: LineSegment StartX=20 StartY=13 StartZ=0 EndX=20 EndY=-13 EndZ=0
    g2: LineSegment StartX=18 StartY=-15 StartZ=0 EndX=17 EndY=-15 EndZ=0
    g3: LineSegment StartX=-20 StartY=-13 StartZ=0 EndX=-20 EndY=13 EndZ=0
    g4: LineSegment StartX=-13 StartY=20 StartZ=0 EndX=13 EndY=20 EndZ=0
    g5: LineSegment StartX=15 StartY=18 StartZ=0 EndX=15 EndY=17 EndZ=0
    g6: LineSegment StartX=13 StartY=-20 StartZ=0 EndX=-13 EndY=-20 EndZ=0
    g7: LineSegment StartX=-15 StartY=-18 StartZ=0 EndX=-15 EndY=-17 EndZ=0
    g8: LineSegment StartX=17 StartY=15 StartZ=0 EndX=18 EndY=15 EndZ=0
    g9: LineSegment StartX=-15 StartY=17 StartZ=0 EndX=-15 EndY=18 EndZ=0
    g10: LineSegment StartX=-17 StartY=-15 StartZ=0 EndX=-18 EndY=-15 EndZ=0
    g11: LineSegment StartX=15 StartY=-17 StartZ=0 EndX=15 EndY=-18 EndZ=0
    g12: ArcOfCircle CenterX=-13 CenterY=-18 CenterZ=0 NormalX=0 NormalY=0 NormalZ=1 AngleXU=0 Radius=2 StartAngle=3.14159 EndAngle=4.71239
    g13: GeomPoint X=-15 Y=-20 Z=0
    g14: ArcOfCircle CenterX=13 CenterY=-18 CenterZ=0 NormalX=0 NormalY=0 NormalZ=1 AngleXU=0 Radius=2 StartAngle=4.71239 EndAngle=6.28319
    g15: GeomPoint X=15 Y=-20 Z=0
    g16: ArcOfCircle CenterX=17 CenterY=-17 CenterZ=0 NormalX=0 NormalY=0 NormalZ=1 AngleXU=0 Radius=2 StartAngle=1.5708 EndAngle=3.14159
    g17: GeomPoint X=15 Y=-15 Z=0
    g18: ArcOfCircle CenterX=18 CenterY=-13 CenterZ=0 NormalX=0 NormalY=0 NormalZ=1 AngleXU=0 Radius=2 StartAngle=4.71239 EndAngle=6.28319
    g19: GeomPoint X=20 Y=-15 Z=0
    g20: ArcOfCircle CenterX=18 CenterY=13 CenterZ=0 NormalX=0 NormalY=0 NormalZ=1 AngleXU=0 Radius=2 StartAngle=0 EndAngle=1.5708
    g21: GeomPoint X=20 Y=15 Z=0
    g22: ArcOfCircle CenterX=17 CenterY=17 CenterZ=0 NormalX=0 NormalY=0 NormalZ=1 AngleXU=0 Radius=2 StartAngle=3.14159 EndAngle=4.71239
    g23: GeomPoint X=15 Y=15 Z=0
    g24: ArcOfCircle CenterX=13 CenterY=18 CenterZ=0 NormalX=0 NormalY=0 NormalZ=1 AngleXU=0 Radius=2 StartAngle=4e-16 EndAngle=1.5708
    g25: GeomPoint X=15 Y=20 Z=0
    g26: ArcOfCircle CenterX=-13 CenterY=18 CenterZ=0 NormalX=0 NormalY=0 NormalZ=1 AngleXU=0 Radius=2 StartAngle=1.5708 EndAngle=3.14159
    g27: GeomPoint X=-15 Y=20 Z=0
    g28: ArcOfCircle CenterX=-17 CenterY=17 CenterZ=0 NormalX=0 NormalY=0 NormalZ=1 AngleXU=0 Radius=2 StartAngle=4.71239 EndAngle=6.28319
    g29: GeomPoint X=-15 Y=15 Z=0
    g30: ArcOfCircle CenterX=-18 CenterY=13 CenterZ=0 NormalX=0 NormalY=0 NormalZ=1 AngleXU=0 Radius=2 StartAngle=1.5708 EndAngle=3.14159
    g31: GeomPoint X=-20 Y=15 Z=0
    g32: ArcOfCircle CenterX=-18 CenterY=-13 CenterZ=0 NormalX=0 NormalY=0 NormalZ=1 AngleXU=0 Radius=2 StartAngle=3.14159 EndAngle=4.71239
    g33: GeomPoint X=-20 Y=-15 Z=0
    g34: ArcOfCircle CenterX=-17 CenterY=-17 CenterZ=0 NormalX=0 NormalY=0 NormalZ=1 AngleXU=0 Radius=2 StartAngle=0 EndAngle=1.5708
    g35: GeomPoint X=-15 Y=-15 Z=0
  constraints (80):
    c: Horizontal(g2)
    c: Vertical(g3)
    c: Symmetric(g21,g31,g-2)
    c: Symmetric(g21,g19,g-1)
    c: DistanceX(g31,g21) = 40
    c: DistanceY(g19,g21) = 30
    c: Horizontal(g4)
    c: Vertical(g7)
    c: Symmetric(g13,g15,g-2)
    c: Symmetric(g15,g25,g-1)
    c: DistanceY(g15,g25) = 40
    c: Vertical(g9)
    c: Vertical(g5)
    c: Vertical(g11)
    c: Horizontal(g10)
    c: Horizontal(g8)
    c: Horizontal(g0)
    c: DistanceX(g13,g15) = 30
    c: DistanceY(g33,g31) = 30
    c: DistanceX(g27,g25) = 30
    c: PointOnObject(g13,g7)
    c: PointOnObject(g13,g6)
    c: Tangent(g7,g12) = 1.5708
    c: Tangent(g6,g12) = 1.5708
    c: Radius(g12) = 2
    c: PointOnObject(g15,g11)
    c: PointOnObject(g15,g6)
    c: Tangent(g11,g14) = 1.5708
    c: Tangent(g6,g14) = 1.5708
    c: PointOnObject(g17,g11)
    c: PointOnObject(g17,g2)
    c: Tangent(g11,g16) = -1.5708
    c: Tangent(g2,g16) = -1.5708
    c: PointOnObject(g19,g2)
    c: PointOnObject(g19,g1)
    c: Tangent(g2,g18) = 1.5708
    c: Tangent(g1,g18) = 1.5708
    c: PointOnObject(g21,g1)
    c: PointOnObject(g21,g8)
    c: Tangent(g1,g20) = 1.5708
    c: Tangent(g8,g20) = 1.5708
    c: PointOnObject(g23,g8)
    c: PointOnObject(g23,g5)
    c: Tangent(g8,g22) = -1.5708
    c: Tangent(g5,g22) = -1.5708
    c: PointOnObject(g25,g5)
    c: PointOnObject(g25,g4)
    c: Tangent(g5,g24) = 1.5708
    c: Tangent(g4,g24) = 1.5708
    c: PointOnObject(g27,g9)
    c: PointOnObject(g27,g4)
    c: Tangent(g9,g26) = 1.5708
    c: Tangent(g4,g26) = 1.5708
    c: PointOnObject(g29,g9)
    c: PointOnObject(g29,g0)
    c: Tangent(g9,g28) = -1.5708
    c: Tangent(g0,g28) = -1.5708
    c: PointOnObject(g31,g0)
    c: PointOnObject(g31,g3)
    c: Tangent(g0,g30) = 1.5708
    c: Tangent(g3,g30) = 1.5708
    c: PointOnObject(g33,g3)
    c: PointOnObject(g33,g10)
    c: Tangent(g3,g32) = 1.5708
    c: Tangent(g10,g32) = 1.5708
    c: PointOnObject(g35,g10)
    c: PointOnObject(g35,g7)
    c: Tangent(g10,g34) = -1.5708
    c: Tangent(g7,g34) = -1.5708
    c: Radius(g34) = 2
    c: Radius(g32) = 2
    c: Radius(g30) = 2
    c: Radius(g28) = 2
    c: Radius(g26) = 2
    c: Radius(g24) = 2
    c: Radius(g22) = 2
    c: Radius(g20) = 2
    c: Radius(g18) = 2
    c: Radius(g16) = 2
    c: Radius(g14) = 2
FEATURE [PartDesign::Pocket] Pocket047
  BaseFeature = -> Pad009
  Direction = (0,0,-1)
  Length = 5
  Length2 = 5
  Profile = -> Sketch056
  ReferenceAxis = -> Sketch056 [N_Axis]
  Type = 1
FEATURE [Sketcher::SketchObject] Sketch057
  ExternalGeometry = -> [Pocket047]
  FullyConstrained = true
  MapMode = 5
  Placement = pos=(25,0,0) rot=(0.57735,0.57735,0.57735;2.0944rad)
  Support = -> [Pocket047]
  sketch-geometry (6):
    g0: LineSegment StartX=-15 StartY=10 StartZ=0 EndX=15 EndY=10 EndZ=0
    g1: LineSegment StartX=20 StartY=5 StartZ=0 EndX=20 EndY=0 EndZ=0
    g2: LineSegment StartX=20 StartY=0 StartZ=0 EndX=-20 EndY=0 EndZ=0
    g3: LineSegment StartX=-20 StartY=0 StartZ=0 EndX=-20 EndY=5 EndZ=0
    g4: ArcOfCircle CenterX=15 CenterY=5 CenterZ=0 NormalX=0 NormalY=0 NormalZ=1 AngleXU=0 Radius=5 StartAngle=1.11001e-11 EndAngle=1.5708
    g5: ArcOfCircle CenterX=-15 CenterY=5 CenterZ=0 NormalX=0 NormalY=0 NormalZ=1 AngleXU=0 Radius=5 StartAngle=1.5708 EndAngle=3.14159
  constraints (15):
    c: Coincident(g1,g2)
    c: Coincident(g2,g3)
    c: Vertical(g1)
    c: Vertical(g3)
    c: PointOnObject(g1,g-1)
    c: Tangent(g1,g4) = 1.5708
    c: Tangent(g0,g4) = 1.5708
    c: Tangent(g0,g5) = 1.5708
    c: Tangent(g3,g5) = 1.5708
    c: Horizontal(g0)
    c: DistanceX(g2,g2) = 40
    c: Symmetric(g2,g1,g-2)
    c: Distance(g-1,g0) = 10
    c: Radius(g5) = 5
    c: Radius(g4) = 5
FEATURE [PartDesign::Pocket] Pocket048
  BaseFeature = -> Pocket047
  Direction = (-1,0,0)
  Length = 5
  Length2 = 5
  Profile = -> Sketch057
  ReferenceAxis = -> Sketch057 [N_Axis]
  Type = 1
FEATURE [Sketcher::SketchObject] Sketch058
  FullyConstrained = true
  MapMode = 5
  Placement = pos=(0,-25,0) rot=(1,0,0;1.5708rad)
  Support = -> [Pocket047]
  sketch-geometry (6):
    g0: LineSegment StartX=-15 StartY=10 StartZ=0 EndX=15 EndY=10 EndZ=0
    g1: LineSegment StartX=20 StartY=5 StartZ=0 EndX=20 EndY=0 EndZ=0
    g2: LineSegment StartX=20 StartY=0 StartZ=0 EndX=-20 EndY=0 EndZ=0
    g3: LineSegment StartX=-20 StartY=0 StartZ=0 EndX=-20 EndY=5 EndZ=0
    g4: ArcOfCircle CenterX=15 CenterY=5 CenterZ=0 NormalX=0 NormalY=0 NormalZ=1 AngleXU=0 Radius=5 StartAngle=1.11e-11 EndAngle=1.5708
    g5: ArcOfCircle CenterX=-15 CenterY=5 CenterZ=0 NormalX=0 NormalY=0 NormalZ=1 AngleXU=0 Radius=5 StartAngle=1.5708 EndAngle=3.14159
  constraints (15):
    c: Coincident(g1,g2)
    c: Coincident(g2,g3)
    c: Horizontal(g0)
    c: Vertical(g1)
    c: Vertical(g3)
    c: Symmetric(g2,g1,g-2)
    c: PointOnObject(g1,g-1)
    c: Tangent(g0,g4) = 1.5708
    c: Tangent(g1,g4) = 1.5708
    c: Tangent(g0,g5) = 1.5708
    c: Tangent(g3,g5) = 1.5708
    c: DistanceX(g2,g2) = 40
    c: Distance(g-1,g0) = 10
    c: Radius(g5) = 5
    c: Radius(g4) = 5
FEATURE [PartDesign::Pocket] Pocket049
  BaseFeature = -> Pocket048
  Direction = (0,1,-2e-16)
  Length = 5
  Length2 = 5
  Profile = -> Sketch058
  ReferenceAxis = -> Sketch058 [N_Axis]
  Type = 1
FEATURE [Sketcher::SketchObject] Sketch059
  FullyConstrained = false
  MapMode = 5
  Placement = pos=(0,0,20) rot=(0,0,1;0rad)
  sketch-geometry (4):
    g0: Circle CenterX=-20 CenterY=20 CenterZ=0 NormalX=0 NormalY=0 NormalZ=1 AngleXU=0 Radius=1.55
    g1: Circle CenterX=20 CenterY=20 CenterZ=0 NormalX=0 NormalY=0 NormalZ=1 AngleXU=0 Radius=1.55
    g2: Circle CenterX=20 CenterY=-20 CenterZ=0 NormalX=0 NormalY=0 NormalZ=1 AngleXU=0 Radius=1.55
    g3: Circle CenterX=-20 CenterY=-20 CenterZ=0 NormalX=0 NormalY=0 NormalZ=1 AngleXU=0 Radius=1.55
  constraints (4):
    c: Diameter(g0) = 3.1
    c: Diameter(g1) = 3.1
    c: Diameter(g2) = 3.1
    c: Diameter(g3) = 3.1
FEATURE [PartDesign::Pocket] Pocket050
  BaseFeature = -> Pocket049
  Direction = (0,0,-1)
  Length = 5
  Length2 = 5
  Profile = -> Sketch059
  ReferenceAxis = -> Sketch059 [N_Axis]
  Type = 0
FEATURE [Sketcher::SketchObject] Sketch060
  ExternalGeometry = -> [Pocket050]
  FullyConstrained = true
  MapMode = 5
  Placement = pos=(0,-25,0) rot=(1,0,0;1.5708rad)
  Support = -> [Pocket050]
  sketch-geometry (2):
    g0: Circle CenterX=-20 CenterY=14 CenterZ=0 NormalX=0 NormalY=0 NormalZ=1 AngleXU=0 Radius=1.4
    g1: Circle CenterX=20 CenterY=14 CenterZ=0 NormalX=0 NormalY=0 NormalZ=1 AngleXU=0 Radius=1.4
  constraints (6):
    c: Diameter(g0) = 2.8
    c: Diameter(g1) = 2.8
    c: Distance(g0,g-5) = 5
    c: Distance(g0,g-3) = 6
    c: Distance(g1,g-3) = 6
    c: Distance(g1,g-4) = 5
FEATURE [PartDesign::Pocket] Pocket051
  BaseFeature = -> Pocket050
  Direction = (0,1,-2e-16)
  Length = 3
  Length2 = 5
  Profile = -> Sketch060
  ReferenceAxis = -> Sketch060 [N_Axis]
  Type = 0
FEATURE [Sketcher::SketchObject] Sketch061
  ExternalGeometry = -> [Pocket051]
  FullyConstrained = true
  MapMode = 5
  Placement = pos=(-25,0,0) rot=(0.57735,-0.57735,-0.57735;2.0944rad)
  Support = -> [Pocket051]
  sketch-geometry (2):
    g0: Circle CenterX=-20 CenterY=14 CenterZ=0 NormalX=0 NormalY=0 NormalZ=1 AngleXU=0 Radius=1.4
    g1: Circle CenterX=20 CenterY=14 CenterZ=0 NormalX=0 NormalY=0 NormalZ=1 AngleXU=0 Radius=1.4
  constraints (6):
    c: Diameter(g0) = 2.8
    c: Diameter(g1) = 2.8
    c: Distance(g0,g-3) = 5
    c: Distance(g0,g-4) = 6
    c: Distance(g1,g-4) = 6
    c: Distance(g1,g-5) = 5
FEATURE [PartDesign::Pocket] Pocket052
  BaseFeature = -> Pocket051
  Direction = (1,0,0)
  Length = 3
  Length2 = 5
  Profile = -> Sketch061
  ReferenceAxis = -> Sketch061 [N_Axis]
  Type = 0
FEATURE [PartDesign::Body] Body010  label="BackplaneBlock008"
  Group = -> [Sketch055,Pad009,Sketch056,Pocket047,Sketch057,Sketch058,Pocket048,Pocket049,Sketch059,Pocket050,Sketch060,Pocket051,Sketch061,Pocket052]
  Origin = -> Origin010
  Placement = pos=(145,145,0) rot=(0,0,1;3.14159rad)
  Tip = -> Pocket052
FEATURE [Part::Box] Box  label="Cube"
  AttacherType = Attacher::AttachEngine3D
  Height = 2
  Length = 10
  Placement = pos=(-10,0,18) rot=(0,0,1;0rad)
  Width = 50
FEATURE [Part::Cylinder] Cylinder
  Angle = 360
  AttacherType = Attacher::AttachEngine3D
  FirstAngle = 0
  Height = 10
  Placement = pos=(-5,12,14) rot=(0,0,1;0rad)
  Radius = 1.55
  SecondAngle = 0
FEATURE [Part::Cylinder] Cylinder001
  Angle = 360
  AttacherType = Attacher::AttachEngine3D
  FirstAngle = 0
  Height = 10
  Placement = pos=(-5,38,14) rot=(0,0,1;0rad)
  Radius = 1.55
  SecondAngle = 0
FEATURE [Part::Cut] Cut
  Base = -> Box
  Tool = -> Cylinder
FEATURE [Part::Cut] Cut001  label="Lip"
  Base = -> Cut
  Placement = pos=(0,170,0) rot=(0,0,1;4.71239rad)
  Tool = -> Cylinder001
FEATURE [App::Link] Link021  label="Lip004"
  LinkPlacement = pos=(60,170,0) rot=(0,0,1;4.71239rad)
  LinkedObject = -> Cut001
  Placement = pos=(60,170,0) rot=(0,0,1;4.71239rad)
FEATURE [App::Link] Link022  label="Lip005"
  LinkPlacement = pos=(120,170,0) rot=(0,0,1;4.71239rad)
  LinkedObject = -> Cut001
  Placement = pos=(120,170,0) rot=(0,0,1;4.71239rad)
FEATURE [App::Part] Part
  Group = -> [Body,Link008,Link009,Link010,Link011,Link012,Link013,Link014,Link015,Link016,Link017,Link018,Body002,Body003,Body004,Body005,Body006,Body007,Body008,Body009,Body010,Box,Cylinder,Cylinder001,Cut,Cut001,Link021,Link022]
  Origin = -> Origin
FEATURE [Part::MultiFuse] Fusion
  Shapes = -> [Body,Link008,Link009,Link010,Link011,Link012,Link013,Link014,Link015,Link016,Link017,Link018,Body002,Body003,Body004,Body005,Body006,Body007,Body008,Body009,Body010,Cut001,Link021,Link022]
FEATURE [Mesh::Feature] Mesh  label="Fusion (Meshed)"
